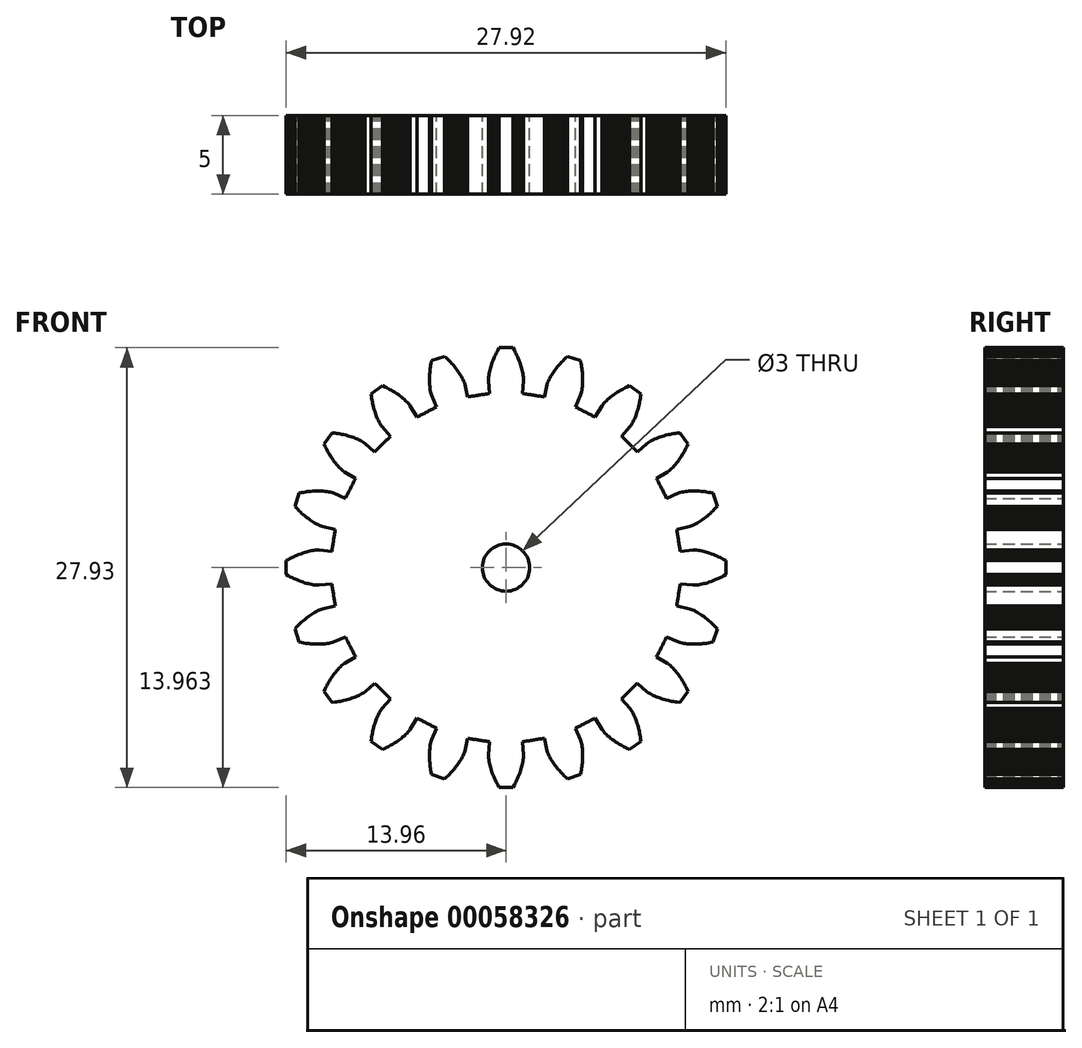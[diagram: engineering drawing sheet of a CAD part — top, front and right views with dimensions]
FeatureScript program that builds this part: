
annotation { "Feature Type Name" : "Feature", "Feature Type Description" : "" }
export const myFeature = defineFeature(function(context is Context, id is Id, definition is map)
    precondition{}
    {
        {
            var Q0;
            Q0=qCreatedBy(makeId("Front.planeOp"),FACE);
            var sketch = newSketch(context, id + "F0", { "sketchPlane" : qUnion([Q0])});
            skLineSegment(sketch, "E0", {"start": v(11.06, 0.88) * mm, "end": v(11.88, 0.8) * mm});
            skLineSegment(sketch, "E1", {"start": v(11.88, 0.8) * mm, "end": v(11.98, 0.8) * mm});
            skLineSegment(sketch, "E2", {"start": v(11.98, 0.8) * mm, "end": v(12.1, 0.8) * mm});
            skLineSegment(sketch, "E3", {"start": v(12.1, 0.8) * mm, "end": v(12.21, 0.82) * mm});
            skLineSegment(sketch, "E4", {"start": v(12.21, 0.82) * mm, "end": v(12.32, 0.84) * mm});
            skLineSegment(sketch, "E5", {"start": v(12.32, 0.84) * mm, "end": v(12.43, 0.86) * mm});
            skLineSegment(sketch, "E6", {"start": v(12.43, 0.86) * mm, "end": v(12.56, 0.9) * mm});
            skLineSegment(sketch, "E7", {"start": v(12.56, 0.9) * mm, "end": v(12.67, 0.92) * mm});
            skLineSegment(sketch, "E8", {"start": v(12.67, 0.92) * mm, "end": v(12.79, 0.95) * mm});
            skLineSegment(sketch, "E9", {"start": v(12.79, 0.95) * mm, "end": v(12.9, 1) * mm});
            skLineSegment(sketch, "E10", {"start": v(12.9, 1) * mm, "end": v(13.03, 1.04) * mm});
            skLineSegment(sketch, "E11", {"start": v(13.03, 1.04) * mm, "end": v(13.17, 1.09) * mm});
            skLineSegment(sketch, "E12", {"start": v(13.17, 1.09) * mm, "end": v(13.3, 1.15) * mm});
            skLineSegment(sketch, "E13", {"start": v(13.3, 1.15) * mm, "end": v(13.4, 1.19) * mm});
            skLineSegment(sketch, "E14", {"start": v(13.4, 1.19) * mm, "end": v(13.5, 1.23) * mm});
            skLineSegment(sketch, "E15", {"start": v(13.5, 1.23) * mm, "end": v(13.6, 1.28) * mm});
            skLineSegment(sketch, "E16", {"start": v(13.6, 1.28) * mm, "end": v(13.7, 1.33) * mm});
            skLineSegment(sketch, "E17", {"start": v(13.7, 1.33) * mm, "end": v(13.81, 1.39) * mm});
            skLineSegment(sketch, "E18", {"start": v(13.81, 1.39) * mm, "end": v(13.96, 1.47) * mm});
            skLineSegment(sketch, "E19", {"start": v(13.96, 1.47) * mm, "end": v(13.96, 2.35) * mm});
            skLineSegment(sketch, "E20", {"start": v(13.96, 2.35) * mm, "end": v(13.81, 2.44) * mm});
            skLineSegment(sketch, "E21", {"start": v(13.81, 2.44) * mm, "end": v(13.7, 2.5) * mm});
            skLineSegment(sketch, "E22", {"start": v(13.7, 2.5) * mm, "end": v(13.6, 2.54) * mm});
            skLineSegment(sketch, "E23", {"start": v(13.6, 2.54) * mm, "end": v(13.5, 2.6) * mm});
            skLineSegment(sketch, "E24", {"start": v(13.5, 2.6) * mm, "end": v(13.4, 2.64) * mm});
            skLineSegment(sketch, "E25", {"start": v(13.4, 2.64) * mm, "end": v(13.3, 2.68) * mm});
            skLineSegment(sketch, "E26", {"start": v(13.3, 2.68) * mm, "end": v(13.17, 2.74) * mm});
            skLineSegment(sketch, "E27", {"start": v(13.17, 2.74) * mm, "end": v(13.03, 2.79) * mm});
            skLineSegment(sketch, "E28", {"start": v(13.03, 2.79) * mm, "end": v(12.9, 2.83) * mm});
            skLineSegment(sketch, "E29", {"start": v(12.9, 2.83) * mm, "end": v(12.79, 2.87) * mm});
            skLineSegment(sketch, "E30", {"start": v(12.79, 2.87) * mm, "end": v(12.67, 2.9) * mm});
            skLineSegment(sketch, "E31", {"start": v(12.67, 2.9) * mm, "end": v(12.56, 2.93) * mm});
            skLineSegment(sketch, "E32", {"start": v(12.56, 2.93) * mm, "end": v(12.43, 2.97) * mm});
            skLineSegment(sketch, "E33", {"start": v(12.43, 2.97) * mm, "end": v(12.32, 2.99) * mm});
            skLineSegment(sketch, "E34", {"start": v(12.32, 2.99) * mm, "end": v(12.21, 3) * mm});
            skLineSegment(sketch, "E35", {"start": v(12.21, 3) * mm, "end": v(12.1, 3.02) * mm});
            skLineSegment(sketch, "E36", {"start": v(12.1, 3.02) * mm, "end": v(11.98, 3.03) * mm});
            skLineSegment(sketch, "E37", {"start": v(11.98, 3.03) * mm, "end": v(11.88, 3.03) * mm});
            skLineSegment(sketch, "E38", {"start": v(11.88, 3.03) * mm, "end": v(11.06, 2.95) * mm});
            skArc(sketch, "E39", {"start": v(11.06, 2.95) * mm, "mid": v(10.95, 3.65) * mm, "end": v(10.84, 4.35) * mm});
            skLineSegment(sketch, "E40", {"start": v(10.84, 4.35) * mm, "end": v(11.64, 4.53) * mm});
            skLineSegment(sketch, "E41", {"start": v(11.64, 4.53) * mm, "end": v(11.74, 4.56) * mm});
            skLineSegment(sketch, "E42", {"start": v(11.74, 4.56) * mm, "end": v(11.85, 4.6) * mm});
            skLineSegment(sketch, "E43", {"start": v(11.85, 4.6) * mm, "end": v(11.95, 4.65) * mm});
            skLineSegment(sketch, "E44", {"start": v(11.95, 4.65) * mm, "end": v(12.05, 4.7) * mm});
            skLineSegment(sketch, "E45", {"start": v(12.05, 4.7) * mm, "end": v(12.15, 4.75) * mm});
            skLineSegment(sketch, "E46", {"start": v(12.15, 4.75) * mm, "end": v(12.27, 4.82) * mm});
            skLineSegment(sketch, "E47", {"start": v(12.27, 4.82) * mm, "end": v(12.36, 4.88) * mm});
            skLineSegment(sketch, "E48", {"start": v(12.36, 4.88) * mm, "end": v(12.46, 4.95) * mm});
            skLineSegment(sketch, "E49", {"start": v(12.46, 4.95) * mm, "end": v(12.56, 5.02) * mm});
            skLineSegment(sketch, "E50", {"start": v(12.56, 5.02) * mm, "end": v(12.67, 5.1) * mm});
            skLineSegment(sketch, "E51", {"start": v(12.67, 5.1) * mm, "end": v(12.78, 5.2) * mm});
            skLineSegment(sketch, "E52", {"start": v(12.78, 5.2) * mm, "end": v(12.9, 5.3) * mm});
            skLineSegment(sketch, "E53", {"start": v(12.9, 5.3) * mm, "end": v(12.97, 5.36) * mm});
            skLineSegment(sketch, "E54", {"start": v(12.97, 5.36) * mm, "end": v(13.05, 5.44) * mm});
            skLineSegment(sketch, "E55", {"start": v(13.05, 5.44) * mm, "end": v(13.13, 5.52) * mm});
            skLineSegment(sketch, "E56", {"start": v(13.13, 5.52) * mm, "end": v(13.22, 5.6) * mm});
            skLineSegment(sketch, "E57", {"start": v(13.22, 5.6) * mm, "end": v(13.3, 5.68) * mm});
            skLineSegment(sketch, "E58", {"start": v(13.3, 5.68) * mm, "end": v(13.42, 5.8) * mm});
            skLineSegment(sketch, "E59", {"start": v(13.42, 5.8) * mm, "end": v(13.14, 6.65) * mm});
            skLineSegment(sketch, "E60", {"start": v(13.14, 6.65) * mm, "end": v(12.98, 6.68) * mm});
            skLineSegment(sketch, "E61", {"start": v(12.98, 6.68) * mm, "end": v(12.86, 6.7) * mm});
            skLineSegment(sketch, "E62", {"start": v(12.86, 6.7) * mm, "end": v(12.74, 6.72) * mm});
            skLineSegment(sketch, "E63", {"start": v(12.74, 6.72) * mm, "end": v(12.63, 6.73) * mm});
            skLineSegment(sketch, "E64", {"start": v(12.63, 6.73) * mm, "end": v(12.52, 6.74) * mm});
            skLineSegment(sketch, "E65", {"start": v(12.52, 6.74) * mm, "end": v(12.42, 6.75) * mm});
            skLineSegment(sketch, "E66", {"start": v(12.42, 6.75) * mm, "end": v(12.27, 6.77) * mm});
            skLineSegment(sketch, "E67", {"start": v(12.27, 6.77) * mm, "end": v(12.12, 6.77) * mm});
            skLineSegment(sketch, "E68", {"start": v(12.12, 6.77) * mm, "end": v(11.99, 6.78) * mm});
            skLineSegment(sketch, "E69", {"start": v(11.99, 6.78) * mm, "end": v(11.86, 6.78) * mm});
            skLineSegment(sketch, "E70", {"start": v(11.86, 6.78) * mm, "end": v(11.74, 6.77) * mm});
            skLineSegment(sketch, "E71", {"start": v(11.74, 6.77) * mm, "end": v(11.63, 6.77) * mm});
            skLineSegment(sketch, "E72", {"start": v(11.63, 6.77) * mm, "end": v(11.5, 6.76) * mm});
            skLineSegment(sketch, "E73", {"start": v(11.5, 6.76) * mm, "end": v(11.38, 6.74) * mm});
            skLineSegment(sketch, "E74", {"start": v(11.38, 6.74) * mm, "end": v(11.28, 6.73) * mm});
            skLineSegment(sketch, "E75", {"start": v(11.28, 6.73) * mm, "end": v(11.17, 6.7) * mm});
            skLineSegment(sketch, "E76", {"start": v(11.17, 6.7) * mm, "end": v(11.05, 6.68) * mm});
            skLineSegment(sketch, "E77", {"start": v(11.05, 6.68) * mm, "end": v(10.96, 6.64) * mm});
            skLineSegment(sketch, "E78", {"start": v(10.96, 6.64) * mm, "end": v(10.2, 6.32) * mm});
            skArc(sketch, "E79", {"start": v(10.2, 6.32) * mm, "mid": v(9.88, 6.95) * mm, "end": v(9.56, 7.58) * mm});
            skLineSegment(sketch, "E80", {"start": v(9.56, 7.58) * mm, "end": v(10.27, 8) * mm});
            skLineSegment(sketch, "E81", {"start": v(10.27, 8) * mm, "end": v(10.35, 8.06) * mm});
            skLineSegment(sketch, "E82", {"start": v(10.35, 8.06) * mm, "end": v(10.44, 8.13) * mm});
            skLineSegment(sketch, "E83", {"start": v(10.44, 8.13) * mm, "end": v(10.52, 8.2) * mm});
            skLineSegment(sketch, "E84", {"start": v(10.52, 8.2) * mm, "end": v(10.6, 8.28) * mm});
            skLineSegment(sketch, "E85", {"start": v(10.6, 8.28) * mm, "end": v(10.68, 8.37) * mm});
            skLineSegment(sketch, "E86", {"start": v(10.68, 8.37) * mm, "end": v(10.77, 8.47) * mm});
            skLineSegment(sketch, "E87", {"start": v(10.77, 8.47) * mm, "end": v(10.84, 8.56) * mm});
            skLineSegment(sketch, "E88", {"start": v(10.84, 8.56) * mm, "end": v(10.9, 8.65) * mm});
            skLineSegment(sketch, "E89", {"start": v(10.9, 8.65) * mm, "end": v(10.98, 8.75) * mm});
            skLineSegment(sketch, "E90", {"start": v(10.98, 8.75) * mm, "end": v(11.06, 8.86) * mm});
            skLineSegment(sketch, "E91", {"start": v(11.06, 8.86) * mm, "end": v(11.14, 8.98) * mm});
            skLineSegment(sketch, "E92", {"start": v(11.14, 8.98) * mm, "end": v(11.22, 9.11) * mm});
            skLineSegment(sketch, "E93", {"start": v(11.22, 9.11) * mm, "end": v(11.27, 9.2) * mm});
            skLineSegment(sketch, "E94", {"start": v(11.27, 9.2) * mm, "end": v(11.32, 9.3) * mm});
            skLineSegment(sketch, "E95", {"start": v(11.32, 9.3) * mm, "end": v(11.38, 9.4) * mm});
            skLineSegment(sketch, "E96", {"start": v(11.38, 9.4) * mm, "end": v(11.43, 9.5) * mm});
            skLineSegment(sketch, "E97", {"start": v(11.43, 9.5) * mm, "end": v(11.48, 9.6) * mm});
            skLineSegment(sketch, "E98", {"start": v(11.48, 9.6) * mm, "end": v(11.56, 9.76) * mm});
            skLineSegment(sketch, "E99", {"start": v(11.56, 9.76) * mm, "end": v(11.04, 10.48) * mm});
            skLineSegment(sketch, "E100", {"start": v(11.04, 10.48) * mm, "end": v(10.87, 10.46) * mm});
            skLineSegment(sketch, "E101", {"start": v(10.87, 10.46) * mm, "end": v(10.75, 10.44) * mm});
            skLineSegment(sketch, "E102", {"start": v(10.75, 10.44) * mm, "end": v(10.64, 10.42) * mm});
            skLineSegment(sketch, "E103", {"start": v(10.64, 10.42) * mm, "end": v(10.52, 10.4) * mm});
            skLineSegment(sketch, "E104", {"start": v(10.52, 10.4) * mm, "end": v(10.42, 10.38) * mm});
            skLineSegment(sketch, "E105", {"start": v(10.42, 10.38) * mm, "end": v(10.31, 10.36) * mm});
            skLineSegment(sketch, "E106", {"start": v(10.31, 10.36) * mm, "end": v(10.17, 10.32) * mm});
            skLineSegment(sketch, "E107", {"start": v(10.17, 10.32) * mm, "end": v(10.03, 10.28) * mm});
            skLineSegment(sketch, "E108", {"start": v(10.03, 10.28) * mm, "end": v(9.9, 10.24) * mm});
            skLineSegment(sketch, "E109", {"start": v(9.9, 10.24) * mm, "end": v(9.78, 10.2) * mm});
            skLineSegment(sketch, "E110", {"start": v(9.78, 10.2) * mm, "end": v(9.67, 10.16) * mm});
            skLineSegment(sketch, "E111", {"start": v(9.67, 10.16) * mm, "end": v(9.56, 10.12) * mm});
            skLineSegment(sketch, "E112", {"start": v(9.56, 10.12) * mm, "end": v(9.44, 10.07) * mm});
            skLineSegment(sketch, "E113", {"start": v(9.44, 10.07) * mm, "end": v(9.33, 10.02) * mm});
            skLineSegment(sketch, "E114", {"start": v(9.33, 10.02) * mm, "end": v(9.24, 9.97) * mm});
            skLineSegment(sketch, "E115", {"start": v(9.24, 9.97) * mm, "end": v(9.14, 9.92) * mm});
            skLineSegment(sketch, "E116", {"start": v(9.14, 9.92) * mm, "end": v(9.04, 9.86) * mm});
            skLineSegment(sketch, "E117", {"start": v(9.04, 9.86) * mm, "end": v(8.96, 9.8) * mm});
            skLineSegment(sketch, "E118", {"start": v(8.96, 9.8) * mm, "end": v(8.34, 9.25) * mm});
            skArc(sketch, "E119", {"start": v(8.34, 9.25) * mm, "mid": v(7.84, 9.75) * mm, "end": v(7.34, 10.25) * mm});
            skLineSegment(sketch, "E120", {"start": v(7.34, 10.25) * mm, "end": v(7.89, 10.87) * mm});
            skLineSegment(sketch, "E121", {"start": v(7.89, 10.87) * mm, "end": v(7.95, 10.95) * mm});
            skLineSegment(sketch, "E122", {"start": v(7.95, 10.95) * mm, "end": v(8, 11.05) * mm});
            skLineSegment(sketch, "E123", {"start": v(8, 11.05) * mm, "end": v(8.06, 11.15) * mm});
            skLineSegment(sketch, "E124", {"start": v(8.06, 11.15) * mm, "end": v(8.1, 11.24) * mm});
            skLineSegment(sketch, "E125", {"start": v(8.1, 11.24) * mm, "end": v(8.16, 11.35) * mm});
            skLineSegment(sketch, "E126", {"start": v(8.16, 11.35) * mm, "end": v(8.21, 11.48) * mm});
            skLineSegment(sketch, "E127", {"start": v(8.21, 11.48) * mm, "end": v(8.25, 11.58) * mm});
            skLineSegment(sketch, "E128", {"start": v(8.25, 11.58) * mm, "end": v(8.3, 11.7) * mm});
            skLineSegment(sketch, "E129", {"start": v(8.3, 11.7) * mm, "end": v(8.33, 11.81) * mm});
            skLineSegment(sketch, "E130", {"start": v(8.33, 11.81) * mm, "end": v(8.37, 11.94) * mm});
            skLineSegment(sketch, "E131", {"start": v(8.37, 11.94) * mm, "end": v(8.4, 12.08) * mm});
            skLineSegment(sketch, "E132", {"start": v(8.4, 12.08) * mm, "end": v(8.44, 12.23) * mm});
            skLineSegment(sketch, "E133", {"start": v(8.44, 12.23) * mm, "end": v(8.47, 12.33) * mm});
            skLineSegment(sketch, "E134", {"start": v(8.47, 12.33) * mm, "end": v(8.49, 12.44) * mm});
            skLineSegment(sketch, "E135", {"start": v(8.49, 12.44) * mm, "end": v(8.5, 12.55) * mm});
            skLineSegment(sketch, "E136", {"start": v(8.5, 12.55) * mm, "end": v(8.53, 12.66) * mm});
            skLineSegment(sketch, "E137", {"start": v(8.53, 12.66) * mm, "end": v(8.54, 12.78) * mm});
            skLineSegment(sketch, "E138", {"start": v(8.54, 12.78) * mm, "end": v(8.56, 12.95) * mm});
            skLineSegment(sketch, "E139", {"start": v(8.56, 12.95) * mm, "end": v(7.85, 13.47) * mm});
            skLineSegment(sketch, "E140", {"start": v(7.85, 13.47) * mm, "end": v(7.7, 13.4) * mm});
            skLineSegment(sketch, "E141", {"start": v(7.7, 13.4) * mm, "end": v(7.59, 13.34) * mm});
            skLineSegment(sketch, "E142", {"start": v(7.59, 13.34) * mm, "end": v(7.49, 13.29) * mm});
            skLineSegment(sketch, "E143", {"start": v(7.49, 13.29) * mm, "end": v(7.39, 13.24) * mm});
            skLineSegment(sketch, "E144", {"start": v(7.39, 13.24) * mm, "end": v(7.3, 13.18) * mm});
            skLineSegment(sketch, "E145", {"start": v(7.3, 13.18) * mm, "end": v(7.2, 13.13) * mm});
            skLineSegment(sketch, "E146", {"start": v(7.2, 13.13) * mm, "end": v(7.07, 13.05) * mm});
            skLineSegment(sketch, "E147", {"start": v(7.07, 13.05) * mm, "end": v(6.95, 12.97) * mm});
            skLineSegment(sketch, "E148", {"start": v(6.95, 12.97) * mm, "end": v(6.84, 12.9) * mm});
            skLineSegment(sketch, "E149", {"start": v(6.84, 12.9) * mm, "end": v(6.74, 12.82) * mm});
            skLineSegment(sketch, "E150", {"start": v(6.74, 12.82) * mm, "end": v(6.64, 12.75) * mm});
            skLineSegment(sketch, "E151", {"start": v(6.64, 12.75) * mm, "end": v(6.56, 12.68) * mm});
            skLineSegment(sketch, "E152", {"start": v(6.56, 12.68) * mm, "end": v(6.46, 12.6) * mm});
            skLineSegment(sketch, "E153", {"start": v(6.46, 12.6) * mm, "end": v(6.37, 12.5) * mm});
            skLineSegment(sketch, "E154", {"start": v(6.37, 12.5) * mm, "end": v(6.3, 12.43) * mm});
            skLineSegment(sketch, "E155", {"start": v(6.3, 12.43) * mm, "end": v(6.22, 12.35) * mm});
            skLineSegment(sketch, "E156", {"start": v(6.22, 12.35) * mm, "end": v(6.14, 12.26) * mm});
            skLineSegment(sketch, "E157", {"start": v(6.14, 12.26) * mm, "end": v(6.08, 12.18) * mm});
            skLineSegment(sketch, "E158", {"start": v(6.08, 12.18) * mm, "end": v(5.66, 11.47) * mm});
            skArc(sketch, "E159", {"start": v(5.66, 11.47) * mm, "mid": v(5.03, 11.8) * mm, "end": v(4.4, 12.11) * mm});
            skLineSegment(sketch, "E160", {"start": v(4.4, 12.11) * mm, "end": v(4.73, 12.87) * mm});
            skLineSegment(sketch, "E161", {"start": v(4.73, 12.87) * mm, "end": v(4.76, 12.97) * mm});
            skLineSegment(sketch, "E162", {"start": v(4.76, 12.97) * mm, "end": v(4.8, 13.08) * mm});
            skLineSegment(sketch, "E163", {"start": v(4.8, 13.08) * mm, "end": v(4.81, 13.19) * mm});
            skLineSegment(sketch, "E164", {"start": v(4.81, 13.19) * mm, "end": v(4.83, 13.3) * mm});
            skLineSegment(sketch, "E165", {"start": v(4.83, 13.3) * mm, "end": v(4.84, 13.41) * mm});
            skLineSegment(sketch, "E166", {"start": v(4.84, 13.41) * mm, "end": v(4.85, 13.55) * mm});
            skLineSegment(sketch, "E167", {"start": v(4.85, 13.55) * mm, "end": v(4.86, 13.66) * mm});
            skLineSegment(sketch, "E168", {"start": v(4.86, 13.66) * mm, "end": v(4.86, 13.78) * mm});
            skLineSegment(sketch, "E169", {"start": v(4.86, 13.78) * mm, "end": v(4.86, 13.9) * mm});
            skLineSegment(sketch, "E170", {"start": v(4.86, 13.9) * mm, "end": v(4.86, 14.04) * mm});
            skLineSegment(sketch, "E171", {"start": v(4.86, 14.04) * mm, "end": v(4.85, 14.18) * mm});
            skLineSegment(sketch, "E172", {"start": v(4.85, 14.18) * mm, "end": v(4.84, 14.33) * mm});
            skLineSegment(sketch, "E173", {"start": v(4.84, 14.33) * mm, "end": v(4.83, 14.44) * mm});
            skLineSegment(sketch, "E174", {"start": v(4.83, 14.44) * mm, "end": v(4.82, 14.54) * mm});
            skLineSegment(sketch, "E175", {"start": v(4.82, 14.54) * mm, "end": v(4.8, 14.66) * mm});
            skLineSegment(sketch, "E176", {"start": v(4.8, 14.66) * mm, "end": v(4.79, 14.77) * mm});
            skLineSegment(sketch, "E177", {"start": v(4.79, 14.77) * mm, "end": v(4.77, 14.89) * mm});
            skLineSegment(sketch, "E178", {"start": v(4.77, 14.89) * mm, "end": v(4.73, 15.06) * mm});
            skLineSegment(sketch, "E179", {"start": v(4.73, 15.06) * mm, "end": v(3.9, 15.33) * mm});
            skLineSegment(sketch, "E180", {"start": v(3.9, 15.33) * mm, "end": v(3.77, 15.21) * mm});
            skLineSegment(sketch, "E181", {"start": v(3.77, 15.21) * mm, "end": v(3.69, 15.13) * mm});
            skLineSegment(sketch, "E182", {"start": v(3.69, 15.13) * mm, "end": v(3.6, 15.05) * mm});
            skLineSegment(sketch, "E183", {"start": v(3.6, 15.05) * mm, "end": v(3.53, 14.96) * mm});
            skLineSegment(sketch, "E184", {"start": v(3.53, 14.96) * mm, "end": v(3.45, 14.88) * mm});
            skLineSegment(sketch, "E185", {"start": v(3.45, 14.88) * mm, "end": v(3.38, 14.8) * mm});
            skLineSegment(sketch, "E186", {"start": v(3.38, 14.8) * mm, "end": v(3.28, 14.7) * mm});
            skLineSegment(sketch, "E187", {"start": v(3.28, 14.7) * mm, "end": v(3.2, 14.58) * mm});
            skLineSegment(sketch, "E188", {"start": v(3.2, 14.58) * mm, "end": v(3.11, 14.47) * mm});
            skLineSegment(sketch, "E189", {"start": v(3.11, 14.47) * mm, "end": v(3.04, 14.37) * mm});
            skLineSegment(sketch, "E190", {"start": v(3.04, 14.37) * mm, "end": v(2.97, 14.27) * mm});
            skLineSegment(sketch, "E191", {"start": v(2.97, 14.27) * mm, "end": v(2.91, 14.18) * mm});
            skLineSegment(sketch, "E192", {"start": v(2.91, 14.18) * mm, "end": v(2.84, 14.06) * mm});
            skLineSegment(sketch, "E193", {"start": v(2.84, 14.06) * mm, "end": v(2.78, 13.96) * mm});
            skLineSegment(sketch, "E194", {"start": v(2.78, 13.96) * mm, "end": v(2.73, 13.86) * mm});
            skLineSegment(sketch, "E195", {"start": v(2.73, 13.86) * mm, "end": v(2.69, 13.76) * mm});
            skLineSegment(sketch, "E196", {"start": v(2.69, 13.76) * mm, "end": v(2.64, 13.65) * mm});
            skLineSegment(sketch, "E197", {"start": v(2.64, 13.65) * mm, "end": v(2.61, 13.56) * mm});
            skLineSegment(sketch, "E198", {"start": v(2.61, 13.56) * mm, "end": v(2.43, 12.76) * mm});
            skArc(sketch, "E199", {"start": v(2.43, 12.76) * mm, "mid": v(1.73, 12.87) * mm, "end": v(1.04, 12.98) * mm});
            skLineSegment(sketch, "E200", {"start": v(1.04, 12.98) * mm, "end": v(1.11, 13.8) * mm});
            skLineSegment(sketch, "E201", {"start": v(1.11, 13.8) * mm, "end": v(1.11, 13.9) * mm});
            skLineSegment(sketch, "E202", {"start": v(1.11, 13.9) * mm, "end": v(1.1, 14.01) * mm});
            skLineSegment(sketch, "E203", {"start": v(1.1, 14.01) * mm, "end": v(1.1, 14.12) * mm});
            skLineSegment(sketch, "E204", {"start": v(1.1, 14.12) * mm, "end": v(1.08, 14.23) * mm});
            skLineSegment(sketch, "E205", {"start": v(1.08, 14.23) * mm, "end": v(1.05, 14.35) * mm});
            skLineSegment(sketch, "E206", {"start": v(1.05, 14.35) * mm, "end": v(1.02, 14.48) * mm});
            skLineSegment(sketch, "E207", {"start": v(1.02, 14.48) * mm, "end": v(1, 14.58) * mm});
            skLineSegment(sketch, "E208", {"start": v(1, 14.58) * mm, "end": v(0.96, 14.7) * mm});
            skLineSegment(sketch, "E209", {"start": v(0.96, 14.7) * mm, "end": v(0.92, 14.82) * mm});
            skLineSegment(sketch, "E210", {"start": v(0.92, 14.82) * mm, "end": v(0.88, 14.95) * mm});
            skLineSegment(sketch, "E211", {"start": v(0.88, 14.95) * mm, "end": v(0.83, 15.08) * mm});
            skLineSegment(sketch, "E212", {"start": v(0.83, 15.08) * mm, "end": v(0.77, 15.22) * mm});
            skLineSegment(sketch, "E213", {"start": v(0.77, 15.22) * mm, "end": v(0.73, 15.32) * mm});
            skLineSegment(sketch, "E214", {"start": v(0.73, 15.32) * mm, "end": v(0.68, 15.42) * mm});
            skLineSegment(sketch, "E215", {"start": v(0.68, 15.42) * mm, "end": v(0.63, 15.52) * mm});
            skLineSegment(sketch, "E216", {"start": v(0.63, 15.52) * mm, "end": v(0.58, 15.62) * mm});
            skLineSegment(sketch, "E217", {"start": v(0.58, 15.62) * mm, "end": v(0.52, 15.73) * mm});
            skLineSegment(sketch, "E218", {"start": v(0.52, 15.73) * mm, "end": v(0.44, 15.88) * mm});
            skLineSegment(sketch, "E219", {"start": v(0.44, 15.88) * mm, "end": v(-0.44, 15.88) * mm});
            skLineSegment(sketch, "E220", {"start": v(-0.44, 15.88) * mm, "end": v(-0.52, 15.73) * mm});
            skLineSegment(sketch, "E221", {"start": v(-0.52, 15.73) * mm, "end": v(-0.58, 15.62) * mm});
            skLineSegment(sketch, "E222", {"start": v(-0.58, 15.62) * mm, "end": v(-0.63, 15.52) * mm});
            skLineSegment(sketch, "E223", {"start": v(-0.63, 15.52) * mm, "end": v(-0.68, 15.42) * mm});
            skLineSegment(sketch, "E224", {"start": v(-0.68, 15.42) * mm, "end": v(-0.73, 15.32) * mm});
            skLineSegment(sketch, "E225", {"start": v(-0.73, 15.32) * mm, "end": v(-0.77, 15.22) * mm});
            skLineSegment(sketch, "E226", {"start": v(-0.77, 15.22) * mm, "end": v(-0.83, 15.08) * mm});
            skLineSegment(sketch, "E227", {"start": v(-0.83, 15.08) * mm, "end": v(-0.88, 14.95) * mm});
            skLineSegment(sketch, "E228", {"start": v(-0.88, 14.95) * mm, "end": v(-0.92, 14.82) * mm});
            skLineSegment(sketch, "E229", {"start": v(-0.92, 14.82) * mm, "end": v(-0.96, 14.7) * mm});
            skLineSegment(sketch, "E230", {"start": v(-0.96, 14.7) * mm, "end": v(-1, 14.58) * mm});
            skLineSegment(sketch, "E231", {"start": v(-1, 14.58) * mm, "end": v(-1.02, 14.48) * mm});
            skLineSegment(sketch, "E232", {"start": v(-1.02, 14.48) * mm, "end": v(-1.05, 14.35) * mm});
            skLineSegment(sketch, "E233", {"start": v(-1.05, 14.35) * mm, "end": v(-1.08, 14.23) * mm});
            skLineSegment(sketch, "E234", {"start": v(-1.08, 14.23) * mm, "end": v(-1.1, 14.12) * mm});
            skLineSegment(sketch, "E235", {"start": v(-1.1, 14.12) * mm, "end": v(-1.1, 14.01) * mm});
            skLineSegment(sketch, "E236", {"start": v(-1.1, 14.01) * mm, "end": v(-1.11, 13.9) * mm});
            skLineSegment(sketch, "E237", {"start": v(-1.11, 13.9) * mm, "end": v(-1.11, 13.8) * mm});
            skLineSegment(sketch, "E238", {"start": v(-1.11, 13.8) * mm, "end": v(-1.04, 12.98) * mm});
            skArc(sketch, "E239", {"start": v(-1.04, 12.98) * mm, "mid": v(-1.73, 12.87) * mm, "end": v(-2.43, 12.76) * mm});
            skLineSegment(sketch, "E240", {"start": v(-2.43, 12.76) * mm, "end": v(-2.61, 13.56) * mm});
            skLineSegment(sketch, "E241", {"start": v(-2.61, 13.56) * mm, "end": v(-2.64, 13.65) * mm});
            skLineSegment(sketch, "E242", {"start": v(-2.64, 13.65) * mm, "end": v(-2.69, 13.76) * mm});
            skLineSegment(sketch, "E243", {"start": v(-2.69, 13.76) * mm, "end": v(-2.73, 13.86) * mm});
            skLineSegment(sketch, "E244", {"start": v(-2.73, 13.86) * mm, "end": v(-2.78, 13.96) * mm});
            skLineSegment(sketch, "E245", {"start": v(-2.78, 13.96) * mm, "end": v(-2.84, 14.06) * mm});
            skLineSegment(sketch, "E246", {"start": v(-2.84, 14.06) * mm, "end": v(-2.91, 14.18) * mm});
            skLineSegment(sketch, "E247", {"start": v(-2.91, 14.18) * mm, "end": v(-2.97, 14.27) * mm});
            skLineSegment(sketch, "E248", {"start": v(-2.97, 14.27) * mm, "end": v(-3.04, 14.37) * mm});
            skLineSegment(sketch, "E249", {"start": v(-3.04, 14.37) * mm, "end": v(-3.11, 14.47) * mm});
            skLineSegment(sketch, "E250", {"start": v(-3.11, 14.47) * mm, "end": v(-3.2, 14.58) * mm});
            skLineSegment(sketch, "E251", {"start": v(-3.2, 14.58) * mm, "end": v(-3.28, 14.7) * mm});
            skLineSegment(sketch, "E252", {"start": v(-3.28, 14.7) * mm, "end": v(-3.38, 14.8) * mm});
            skLineSegment(sketch, "E253", {"start": v(-3.38, 14.8) * mm, "end": v(-3.45, 14.88) * mm});
            skLineSegment(sketch, "E254", {"start": v(-3.45, 14.88) * mm, "end": v(-3.53, 14.96) * mm});
            skLineSegment(sketch, "E255", {"start": v(-3.53, 14.96) * mm, "end": v(-3.6, 15.05) * mm});
            skLineSegment(sketch, "E256", {"start": v(-3.6, 15.05) * mm, "end": v(-3.69, 15.13) * mm});
            skLineSegment(sketch, "E257", {"start": v(-3.69, 15.13) * mm, "end": v(-3.77, 15.21) * mm});
            skLineSegment(sketch, "E258", {"start": v(-3.77, 15.21) * mm, "end": v(-3.9, 15.33) * mm});
            skLineSegment(sketch, "E259", {"start": v(-3.9, 15.33) * mm, "end": v(-4.73, 15.06) * mm});
            skLineSegment(sketch, "E260", {"start": v(-4.73, 15.06) * mm, "end": v(-4.77, 14.89) * mm});
            skLineSegment(sketch, "E261", {"start": v(-4.77, 14.89) * mm, "end": v(-4.79, 14.77) * mm});
            skLineSegment(sketch, "E262", {"start": v(-4.79, 14.77) * mm, "end": v(-4.8, 14.66) * mm});
            skLineSegment(sketch, "E263", {"start": v(-4.8, 14.66) * mm, "end": v(-4.82, 14.54) * mm});
            skLineSegment(sketch, "E264", {"start": v(-4.82, 14.54) * mm, "end": v(-4.83, 14.44) * mm});
            skLineSegment(sketch, "E265", {"start": v(-4.83, 14.44) * mm, "end": v(-4.84, 14.33) * mm});
            skLineSegment(sketch, "E266", {"start": v(-4.84, 14.33) * mm, "end": v(-4.85, 14.18) * mm});
            skLineSegment(sketch, "E267", {"start": v(-4.85, 14.18) * mm, "end": v(-4.86, 14.04) * mm});
            skLineSegment(sketch, "E268", {"start": v(-4.86, 14.04) * mm, "end": v(-4.86, 13.9) * mm});
            skLineSegment(sketch, "E269", {"start": v(-4.86, 13.9) * mm, "end": v(-4.86, 13.78) * mm});
            skLineSegment(sketch, "E270", {"start": v(-4.86, 13.78) * mm, "end": v(-4.86, 13.66) * mm});
            skLineSegment(sketch, "E271", {"start": v(-4.86, 13.66) * mm, "end": v(-4.85, 13.55) * mm});
            skLineSegment(sketch, "E272", {"start": v(-4.85, 13.55) * mm, "end": v(-4.84, 13.41) * mm});
            skLineSegment(sketch, "E273", {"start": v(-4.84, 13.41) * mm, "end": v(-4.83, 13.3) * mm});
            skLineSegment(sketch, "E274", {"start": v(-4.83, 13.3) * mm, "end": v(-4.81, 13.19) * mm});
            skLineSegment(sketch, "E275", {"start": v(-4.81, 13.19) * mm, "end": v(-4.8, 13.08) * mm});
            skLineSegment(sketch, "E276", {"start": v(-4.8, 13.08) * mm, "end": v(-4.76, 12.97) * mm});
            skLineSegment(sketch, "E277", {"start": v(-4.76, 12.97) * mm, "end": v(-4.73, 12.87) * mm});
            skLineSegment(sketch, "E278", {"start": v(-4.73, 12.87) * mm, "end": v(-4.4, 12.11) * mm});
            skArc(sketch, "E279", {"start": v(-4.4, 12.11) * mm, "mid": v(-5.03, 11.8) * mm, "end": v(-5.66, 11.47) * mm});
            skLineSegment(sketch, "E280", {"start": v(-5.66, 11.47) * mm, "end": v(-6.08, 12.18) * mm});
            skLineSegment(sketch, "E281", {"start": v(-6.08, 12.18) * mm, "end": v(-6.14, 12.26) * mm});
            skLineSegment(sketch, "E282", {"start": v(-6.14, 12.26) * mm, "end": v(-6.22, 12.35) * mm});
            skLineSegment(sketch, "E283", {"start": v(-6.22, 12.35) * mm, "end": v(-6.3, 12.43) * mm});
            skLineSegment(sketch, "E284", {"start": v(-6.3, 12.43) * mm, "end": v(-6.37, 12.5) * mm});
            skLineSegment(sketch, "E285", {"start": v(-6.37, 12.5) * mm, "end": v(-6.46, 12.6) * mm});
            skLineSegment(sketch, "E286", {"start": v(-6.46, 12.6) * mm, "end": v(-6.56, 12.68) * mm});
            skLineSegment(sketch, "E287", {"start": v(-6.56, 12.68) * mm, "end": v(-6.64, 12.75) * mm});
            skLineSegment(sketch, "E288", {"start": v(-6.64, 12.75) * mm, "end": v(-6.74, 12.82) * mm});
            skLineSegment(sketch, "E289", {"start": v(-6.74, 12.82) * mm, "end": v(-6.84, 12.9) * mm});
            skLineSegment(sketch, "E290", {"start": v(-6.84, 12.9) * mm, "end": v(-6.95, 12.97) * mm});
            skLineSegment(sketch, "E291", {"start": v(-6.95, 12.97) * mm, "end": v(-7.07, 13.05) * mm});
            skLineSegment(sketch, "E292", {"start": v(-7.07, 13.05) * mm, "end": v(-7.2, 13.13) * mm});
            skLineSegment(sketch, "E293", {"start": v(-7.2, 13.13) * mm, "end": v(-7.3, 13.18) * mm});
            skLineSegment(sketch, "E294", {"start": v(-7.3, 13.18) * mm, "end": v(-7.39, 13.24) * mm});
            skLineSegment(sketch, "E295", {"start": v(-7.39, 13.24) * mm, "end": v(-7.49, 13.29) * mm});
            skLineSegment(sketch, "E296", {"start": v(-7.49, 13.29) * mm, "end": v(-7.59, 13.34) * mm});
            skLineSegment(sketch, "E297", {"start": v(-7.59, 13.34) * mm, "end": v(-7.7, 13.4) * mm});
            skLineSegment(sketch, "E298", {"start": v(-7.7, 13.4) * mm, "end": v(-7.85, 13.47) * mm});
            skLineSegment(sketch, "E299", {"start": v(-7.85, 13.47) * mm, "end": v(-8.56, 12.95) * mm});
            skLineSegment(sketch, "E300", {"start": v(-8.56, 12.95) * mm, "end": v(-8.54, 12.78) * mm});
            skLineSegment(sketch, "E301", {"start": v(-8.54, 12.78) * mm, "end": v(-8.53, 12.66) * mm});
            skLineSegment(sketch, "E302", {"start": v(-8.53, 12.66) * mm, "end": v(-8.5, 12.55) * mm});
            skLineSegment(sketch, "E303", {"start": v(-8.5, 12.55) * mm, "end": v(-8.49, 12.44) * mm});
            skLineSegment(sketch, "E304", {"start": v(-8.49, 12.44) * mm, "end": v(-8.47, 12.33) * mm});
            skLineSegment(sketch, "E305", {"start": v(-8.47, 12.33) * mm, "end": v(-8.44, 12.23) * mm});
            skLineSegment(sketch, "E306", {"start": v(-8.44, 12.23) * mm, "end": v(-8.4, 12.08) * mm});
            skLineSegment(sketch, "E307", {"start": v(-8.4, 12.08) * mm, "end": v(-8.37, 11.94) * mm});
            skLineSegment(sketch, "E308", {"start": v(-8.37, 11.94) * mm, "end": v(-8.33, 11.81) * mm});
            skLineSegment(sketch, "E309", {"start": v(-8.33, 11.81) * mm, "end": v(-8.3, 11.7) * mm});
            skLineSegment(sketch, "E310", {"start": v(-8.3, 11.7) * mm, "end": v(-8.25, 11.58) * mm});
            skLineSegment(sketch, "E311", {"start": v(-8.25, 11.58) * mm, "end": v(-8.21, 11.48) * mm});
            skLineSegment(sketch, "E312", {"start": v(-8.21, 11.48) * mm, "end": v(-8.16, 11.35) * mm});
            skLineSegment(sketch, "E313", {"start": v(-8.16, 11.35) * mm, "end": v(-8.1, 11.24) * mm});
            skLineSegment(sketch, "E314", {"start": v(-8.1, 11.24) * mm, "end": v(-8.06, 11.15) * mm});
            skLineSegment(sketch, "E315", {"start": v(-8.06, 11.15) * mm, "end": v(-8, 11.05) * mm});
            skLineSegment(sketch, "E316", {"start": v(-8, 11.05) * mm, "end": v(-7.95, 10.95) * mm});
            skLineSegment(sketch, "E317", {"start": v(-7.95, 10.95) * mm, "end": v(-7.89, 10.87) * mm});
            skLineSegment(sketch, "E318", {"start": v(-7.89, 10.87) * mm, "end": v(-7.34, 10.25) * mm});
            skArc(sketch, "E319", {"start": v(-7.34, 10.25) * mm, "mid": v(-7.84, 9.75) * mm, "end": v(-8.34, 9.25) * mm});
            skLineSegment(sketch, "E320", {"start": v(-8.34, 9.25) * mm, "end": v(-8.96, 9.8) * mm});
            skLineSegment(sketch, "E321", {"start": v(-8.96, 9.8) * mm, "end": v(-9.04, 9.86) * mm});
            skLineSegment(sketch, "E322", {"start": v(-9.04, 9.86) * mm, "end": v(-9.14, 9.92) * mm});
            skLineSegment(sketch, "E323", {"start": v(-9.14, 9.92) * mm, "end": v(-9.24, 9.97) * mm});
            skLineSegment(sketch, "E324", {"start": v(-9.24, 9.97) * mm, "end": v(-9.33, 10.02) * mm});
            skLineSegment(sketch, "E325", {"start": v(-9.33, 10.02) * mm, "end": v(-9.44, 10.07) * mm});
            skLineSegment(sketch, "E326", {"start": v(-9.44, 10.07) * mm, "end": v(-9.56, 10.12) * mm});
            skLineSegment(sketch, "E327", {"start": v(-9.56, 10.12) * mm, "end": v(-9.67, 10.16) * mm});
            skLineSegment(sketch, "E328", {"start": v(-9.67, 10.16) * mm, "end": v(-9.78, 10.2) * mm});
            skLineSegment(sketch, "E329", {"start": v(-9.78, 10.2) * mm, "end": v(-9.9, 10.24) * mm});
            skLineSegment(sketch, "E330", {"start": v(-9.9, 10.24) * mm, "end": v(-10.03, 10.28) * mm});
            skLineSegment(sketch, "E331", {"start": v(-10.03, 10.28) * mm, "end": v(-10.17, 10.32) * mm});
            skLineSegment(sketch, "E332", {"start": v(-10.17, 10.32) * mm, "end": v(-10.31, 10.36) * mm});
            skLineSegment(sketch, "E333", {"start": v(-10.31, 10.36) * mm, "end": v(-10.42, 10.38) * mm});
            skLineSegment(sketch, "E334", {"start": v(-10.42, 10.38) * mm, "end": v(-10.52, 10.4) * mm});
            skLineSegment(sketch, "E335", {"start": v(-10.52, 10.4) * mm, "end": v(-10.64, 10.42) * mm});
            skLineSegment(sketch, "E336", {"start": v(-10.64, 10.42) * mm, "end": v(-10.75, 10.44) * mm});
            skLineSegment(sketch, "E337", {"start": v(-10.75, 10.44) * mm, "end": v(-10.87, 10.46) * mm});
            skLineSegment(sketch, "E338", {"start": v(-10.87, 10.46) * mm, "end": v(-11.04, 10.48) * mm});
            skLineSegment(sketch, "E339", {"start": v(-11.04, 10.48) * mm, "end": v(-11.56, 9.76) * mm});
            skLineSegment(sketch, "E340", {"start": v(-11.56, 9.76) * mm, "end": v(-11.48, 9.6) * mm});
            skLineSegment(sketch, "E341", {"start": v(-11.48, 9.6) * mm, "end": v(-11.43, 9.5) * mm});
            skLineSegment(sketch, "E342", {"start": v(-11.43, 9.5) * mm, "end": v(-11.38, 9.4) * mm});
            skLineSegment(sketch, "E343", {"start": v(-11.38, 9.4) * mm, "end": v(-11.32, 9.3) * mm});
            skLineSegment(sketch, "E344", {"start": v(-11.32, 9.3) * mm, "end": v(-11.27, 9.2) * mm});
            skLineSegment(sketch, "E345", {"start": v(-11.27, 9.2) * mm, "end": v(-11.22, 9.11) * mm});
            skLineSegment(sketch, "E346", {"start": v(-11.22, 9.11) * mm, "end": v(-11.14, 8.98) * mm});
            skLineSegment(sketch, "E347", {"start": v(-11.14, 8.98) * mm, "end": v(-11.06, 8.86) * mm});
            skLineSegment(sketch, "E348", {"start": v(-11.06, 8.86) * mm, "end": v(-10.98, 8.75) * mm});
            skLineSegment(sketch, "E349", {"start": v(-10.98, 8.75) * mm, "end": v(-10.9, 8.65) * mm});
            skLineSegment(sketch, "E350", {"start": v(-10.9, 8.65) * mm, "end": v(-10.84, 8.56) * mm});
            skLineSegment(sketch, "E351", {"start": v(-10.84, 8.56) * mm, "end": v(-10.77, 8.47) * mm});
            skLineSegment(sketch, "E352", {"start": v(-10.77, 8.47) * mm, "end": v(-10.68, 8.37) * mm});
            skLineSegment(sketch, "E353", {"start": v(-10.68, 8.37) * mm, "end": v(-10.6, 8.28) * mm});
            skLineSegment(sketch, "E354", {"start": v(-10.6, 8.28) * mm, "end": v(-10.52, 8.2) * mm});
            skLineSegment(sketch, "E355", {"start": v(-10.52, 8.2) * mm, "end": v(-10.44, 8.13) * mm});
            skLineSegment(sketch, "E356", {"start": v(-10.44, 8.13) * mm, "end": v(-10.35, 8.06) * mm});
            skLineSegment(sketch, "E357", {"start": v(-10.35, 8.06) * mm, "end": v(-10.27, 8) * mm});
            skLineSegment(sketch, "E358", {"start": v(-10.27, 8) * mm, "end": v(-9.56, 7.58) * mm});
            skArc(sketch, "E359", {"start": v(-9.56, 7.58) * mm, "mid": v(-9.88, 6.95) * mm, "end": v(-10.2, 6.32) * mm});
            skLineSegment(sketch, "E360", {"start": v(-10.2, 6.32) * mm, "end": v(-10.96, 6.64) * mm});
            skLineSegment(sketch, "E361", {"start": v(-10.96, 6.64) * mm, "end": v(-11.05, 6.68) * mm});
            skLineSegment(sketch, "E362", {"start": v(-11.05, 6.68) * mm, "end": v(-11.17, 6.7) * mm});
            skLineSegment(sketch, "E363", {"start": v(-11.17, 6.7) * mm, "end": v(-11.28, 6.73) * mm});
            skLineSegment(sketch, "E364", {"start": v(-11.28, 6.73) * mm, "end": v(-11.38, 6.74) * mm});
            skLineSegment(sketch, "E365", {"start": v(-11.38, 6.74) * mm, "end": v(-11.5, 6.76) * mm});
            skLineSegment(sketch, "E366", {"start": v(-11.5, 6.76) * mm, "end": v(-11.63, 6.77) * mm});
            skLineSegment(sketch, "E367", {"start": v(-11.63, 6.77) * mm, "end": v(-11.74, 6.77) * mm});
            skLineSegment(sketch, "E368", {"start": v(-11.74, 6.77) * mm, "end": v(-11.86, 6.78) * mm});
            skLineSegment(sketch, "E369", {"start": v(-11.86, 6.78) * mm, "end": v(-11.99, 6.78) * mm});
            skLineSegment(sketch, "E370", {"start": v(-11.99, 6.78) * mm, "end": v(-12.12, 6.77) * mm});
            skLineSegment(sketch, "E371", {"start": v(-12.12, 6.77) * mm, "end": v(-12.27, 6.77) * mm});
            skLineSegment(sketch, "E372", {"start": v(-12.27, 6.77) * mm, "end": v(-12.42, 6.75) * mm});
            skLineSegment(sketch, "E373", {"start": v(-12.42, 6.75) * mm, "end": v(-12.52, 6.74) * mm});
            skLineSegment(sketch, "E374", {"start": v(-12.52, 6.74) * mm, "end": v(-12.63, 6.73) * mm});
            skLineSegment(sketch, "E375", {"start": v(-12.63, 6.73) * mm, "end": v(-12.74, 6.72) * mm});
            skLineSegment(sketch, "E376", {"start": v(-12.74, 6.72) * mm, "end": v(-12.86, 6.7) * mm});
            skLineSegment(sketch, "E377", {"start": v(-12.86, 6.7) * mm, "end": v(-12.98, 6.68) * mm});
            skLineSegment(sketch, "E378", {"start": v(-12.98, 6.68) * mm, "end": v(-13.14, 6.65) * mm});
            skLineSegment(sketch, "E379", {"start": v(-13.14, 6.65) * mm, "end": v(-13.42, 5.8) * mm});
            skLineSegment(sketch, "E380", {"start": v(-13.42, 5.8) * mm, "end": v(-13.3, 5.68) * mm});
            skLineSegment(sketch, "E381", {"start": v(-13.3, 5.68) * mm, "end": v(-13.22, 5.6) * mm});
            skLineSegment(sketch, "E382", {"start": v(-13.22, 5.6) * mm, "end": v(-13.13, 5.52) * mm});
            skLineSegment(sketch, "E383", {"start": v(-13.13, 5.52) * mm, "end": v(-13.05, 5.44) * mm});
            skLineSegment(sketch, "E384", {"start": v(-13.05, 5.44) * mm, "end": v(-12.97, 5.36) * mm});
            skLineSegment(sketch, "E385", {"start": v(-12.97, 5.36) * mm, "end": v(-12.9, 5.3) * mm});
            skLineSegment(sketch, "E386", {"start": v(-12.9, 5.3) * mm, "end": v(-12.78, 5.2) * mm});
            skLineSegment(sketch, "E387", {"start": v(-12.78, 5.2) * mm, "end": v(-12.67, 5.1) * mm});
            skLineSegment(sketch, "E388", {"start": v(-12.67, 5.1) * mm, "end": v(-12.56, 5.02) * mm});
            skLineSegment(sketch, "E389", {"start": v(-12.56, 5.02) * mm, "end": v(-12.46, 4.95) * mm});
            skLineSegment(sketch, "E390", {"start": v(-12.46, 4.95) * mm, "end": v(-12.36, 4.88) * mm});
            skLineSegment(sketch, "E391", {"start": v(-12.36, 4.88) * mm, "end": v(-12.27, 4.82) * mm});
            skLineSegment(sketch, "E392", {"start": v(-12.27, 4.82) * mm, "end": v(-12.15, 4.75) * mm});
            skLineSegment(sketch, "E393", {"start": v(-12.15, 4.75) * mm, "end": v(-12.05, 4.7) * mm});
            skLineSegment(sketch, "E394", {"start": v(-12.05, 4.7) * mm, "end": v(-11.95, 4.65) * mm});
            skLineSegment(sketch, "E395", {"start": v(-11.95, 4.65) * mm, "end": v(-11.85, 4.6) * mm});
            skLineSegment(sketch, "E396", {"start": v(-11.85, 4.6) * mm, "end": v(-11.74, 4.56) * mm});
            skLineSegment(sketch, "E397", {"start": v(-11.74, 4.56) * mm, "end": v(-11.64, 4.53) * mm});
            skLineSegment(sketch, "E398", {"start": v(-11.64, 4.53) * mm, "end": v(-10.84, 4.35) * mm});
            skArc(sketch, "E399", {"start": v(-10.84, 4.35) * mm, "mid": v(-10.95, 3.65) * mm, "end": v(-11.06, 2.95) * mm});
            skLineSegment(sketch, "E400", {"start": v(-11.06, 2.95) * mm, "end": v(-11.88, 3.03) * mm});
            skLineSegment(sketch, "E401", {"start": v(-11.88, 3.03) * mm, "end": v(-11.98, 3.03) * mm});
            skLineSegment(sketch, "E402", {"start": v(-11.98, 3.03) * mm, "end": v(-12.1, 3.02) * mm});
            skLineSegment(sketch, "E403", {"start": v(-12.1, 3.02) * mm, "end": v(-12.21, 3) * mm});
            skLineSegment(sketch, "E404", {"start": v(-12.21, 3) * mm, "end": v(-12.32, 2.99) * mm});
            skLineSegment(sketch, "E405", {"start": v(-12.32, 2.99) * mm, "end": v(-12.43, 2.97) * mm});
            skLineSegment(sketch, "E406", {"start": v(-12.43, 2.97) * mm, "end": v(-12.56, 2.93) * mm});
            skLineSegment(sketch, "E407", {"start": v(-12.56, 2.93) * mm, "end": v(-12.67, 2.9) * mm});
            skLineSegment(sketch, "E408", {"start": v(-12.67, 2.9) * mm, "end": v(-12.79, 2.87) * mm});
            skLineSegment(sketch, "E409", {"start": v(-12.79, 2.87) * mm, "end": v(-12.9, 2.83) * mm});
            skLineSegment(sketch, "E410", {"start": v(-12.9, 2.83) * mm, "end": v(-13.03, 2.79) * mm});
            skLineSegment(sketch, "E411", {"start": v(-13.03, 2.79) * mm, "end": v(-13.17, 2.74) * mm});
            skLineSegment(sketch, "E412", {"start": v(-13.17, 2.74) * mm, "end": v(-13.3, 2.68) * mm});
            skLineSegment(sketch, "E413", {"start": v(-13.3, 2.68) * mm, "end": v(-13.4, 2.64) * mm});
            skLineSegment(sketch, "E414", {"start": v(-13.4, 2.64) * mm, "end": v(-13.5, 2.6) * mm});
            skLineSegment(sketch, "E415", {"start": v(-13.5, 2.6) * mm, "end": v(-13.6, 2.54) * mm});
            skLineSegment(sketch, "E416", {"start": v(-13.6, 2.54) * mm, "end": v(-13.7, 2.5) * mm});
            skLineSegment(sketch, "E417", {"start": v(-13.7, 2.5) * mm, "end": v(-13.81, 2.44) * mm});
            skLineSegment(sketch, "E418", {"start": v(-13.81, 2.44) * mm, "end": v(-13.96, 2.35) * mm});
            skLineSegment(sketch, "E419", {"start": v(-13.96, 2.35) * mm, "end": v(-13.96, 1.47) * mm});
            skLineSegment(sketch, "E420", {"start": v(-13.96, 1.47) * mm, "end": v(-13.81, 1.39) * mm});
            skLineSegment(sketch, "E421", {"start": v(-13.81, 1.39) * mm, "end": v(-13.7, 1.33) * mm});
            skLineSegment(sketch, "E422", {"start": v(-13.7, 1.33) * mm, "end": v(-13.6, 1.28) * mm});
            skLineSegment(sketch, "E423", {"start": v(-13.6, 1.28) * mm, "end": v(-13.5, 1.23) * mm});
            skLineSegment(sketch, "E424", {"start": v(-13.5, 1.23) * mm, "end": v(-13.4, 1.19) * mm});
            skLineSegment(sketch, "E425", {"start": v(-13.4, 1.19) * mm, "end": v(-13.3, 1.15) * mm});
            skLineSegment(sketch, "E426", {"start": v(-13.3, 1.15) * mm, "end": v(-13.17, 1.09) * mm});
            skLineSegment(sketch, "E427", {"start": v(-13.17, 1.09) * mm, "end": v(-13.03, 1.04) * mm});
            skLineSegment(sketch, "E428", {"start": v(-13.03, 1.04) * mm, "end": v(-12.9, 1) * mm});
            skLineSegment(sketch, "E429", {"start": v(-12.9, 1) * mm, "end": v(-12.79, 0.95) * mm});
            skLineSegment(sketch, "E430", {"start": v(-12.79, 0.95) * mm, "end": v(-12.67, 0.92) * mm});
            skLineSegment(sketch, "E431", {"start": v(-12.67, 0.92) * mm, "end": v(-12.56, 0.9) * mm});
            skLineSegment(sketch, "E432", {"start": v(-12.56, 0.9) * mm, "end": v(-12.43, 0.86) * mm});
            skLineSegment(sketch, "E433", {"start": v(-12.43, 0.86) * mm, "end": v(-12.32, 0.84) * mm});
            skLineSegment(sketch, "E434", {"start": v(-12.32, 0.84) * mm, "end": v(-12.21, 0.82) * mm});
            skLineSegment(sketch, "E435", {"start": v(-12.21, 0.82) * mm, "end": v(-12.1, 0.8) * mm});
            skLineSegment(sketch, "E436", {"start": v(-12.1, 0.8) * mm, "end": v(-11.98, 0.8) * mm});
            skLineSegment(sketch, "E437", {"start": v(-11.98, 0.8) * mm, "end": v(-11.88, 0.8) * mm});
            skLineSegment(sketch, "E438", {"start": v(-11.88, 0.8) * mm, "end": v(-11.06, 0.88) * mm});
            skArc(sketch, "E439", {"start": v(-11.06, 0.88) * mm, "mid": v(-10.95, 0.18) * mm, "end": v(-10.84, -0.52) * mm});
            skLineSegment(sketch, "E440", {"start": v(-10.84, -0.52) * mm, "end": v(-11.64, -0.7) * mm});
            skLineSegment(sketch, "E441", {"start": v(-11.64, -0.7) * mm, "end": v(-11.74, -0.73) * mm});
            skLineSegment(sketch, "E442", {"start": v(-11.74, -0.73) * mm, "end": v(-11.85, -0.77) * mm});
            skLineSegment(sketch, "E443", {"start": v(-11.85, -0.77) * mm, "end": v(-11.95, -0.82) * mm});
            skLineSegment(sketch, "E444", {"start": v(-11.95, -0.82) * mm, "end": v(-12.05, -0.87) * mm});
            skLineSegment(sketch, "E445", {"start": v(-12.05, -0.87) * mm, "end": v(-12.15, -0.93) * mm});
            skLineSegment(sketch, "E446", {"start": v(-12.15, -0.93) * mm, "end": v(-12.27, -1) * mm});
            skLineSegment(sketch, "E447", {"start": v(-12.27, -1) * mm, "end": v(-12.36, -1.06) * mm});
            skLineSegment(sketch, "E448", {"start": v(-12.36, -1.06) * mm, "end": v(-12.46, -1.13) * mm});
            skLineSegment(sketch, "E449", {"start": v(-12.46, -1.13) * mm, "end": v(-12.56, -1.2) * mm});
            skLineSegment(sketch, "E450", {"start": v(-12.56, -1.2) * mm, "end": v(-12.67, -1.28) * mm});
            skLineSegment(sketch, "E451", {"start": v(-12.67, -1.28) * mm, "end": v(-12.78, -1.37) * mm});
            skLineSegment(sketch, "E452", {"start": v(-12.78, -1.37) * mm, "end": v(-12.9, -1.47) * mm});
            skLineSegment(sketch, "E453", {"start": v(-12.9, -1.47) * mm, "end": v(-12.97, -1.54) * mm});
            skLineSegment(sketch, "E454", {"start": v(-12.97, -1.54) * mm, "end": v(-13.05, -1.61) * mm});
            skLineSegment(sketch, "E455", {"start": v(-13.05, -1.61) * mm, "end": v(-13.13, -1.7) * mm});
            skLineSegment(sketch, "E456", {"start": v(-13.13, -1.7) * mm, "end": v(-13.22, -1.77) * mm});
            skLineSegment(sketch, "E457", {"start": v(-13.22, -1.77) * mm, "end": v(-13.3, -1.86) * mm});
            skLineSegment(sketch, "E458", {"start": v(-13.3, -1.86) * mm, "end": v(-13.42, -1.98) * mm});
            skLineSegment(sketch, "E459", {"start": v(-13.42, -1.98) * mm, "end": v(-13.14, -2.82) * mm});
            skLineSegment(sketch, "E460", {"start": v(-13.14, -2.82) * mm, "end": v(-12.98, -2.85) * mm});
            skLineSegment(sketch, "E461", {"start": v(-12.98, -2.85) * mm, "end": v(-12.86, -2.87) * mm});
            skLineSegment(sketch, "E462", {"start": v(-12.86, -2.87) * mm, "end": v(-12.74, -2.9) * mm});
            skLineSegment(sketch, "E463", {"start": v(-12.74, -2.9) * mm, "end": v(-12.63, -2.9) * mm});
            skLineSegment(sketch, "E464", {"start": v(-12.63, -2.9) * mm, "end": v(-12.52, -2.92) * mm});
            skLineSegment(sketch, "E465", {"start": v(-12.52, -2.92) * mm, "end": v(-12.42, -2.93) * mm});
            skLineSegment(sketch, "E466", {"start": v(-12.42, -2.93) * mm, "end": v(-12.27, -2.94) * mm});
            skLineSegment(sketch, "E467", {"start": v(-12.27, -2.94) * mm, "end": v(-12.12, -2.95) * mm});
            skLineSegment(sketch, "E468", {"start": v(-12.12, -2.95) * mm, "end": v(-11.99, -2.95) * mm});
            skLineSegment(sketch, "E469", {"start": v(-11.99, -2.95) * mm, "end": v(-11.86, -2.95) * mm});
            skLineSegment(sketch, "E470", {"start": v(-11.86, -2.95) * mm, "end": v(-11.74, -2.95) * mm});
            skLineSegment(sketch, "E471", {"start": v(-11.74, -2.95) * mm, "end": v(-11.63, -2.94) * mm});
            skLineSegment(sketch, "E472", {"start": v(-11.63, -2.94) * mm, "end": v(-11.5, -2.93) * mm});
            skLineSegment(sketch, "E473", {"start": v(-11.5, -2.93) * mm, "end": v(-11.38, -2.92) * mm});
            skLineSegment(sketch, "E474", {"start": v(-11.38, -2.92) * mm, "end": v(-11.28, -2.9) * mm});
            skLineSegment(sketch, "E475", {"start": v(-11.28, -2.9) * mm, "end": v(-11.17, -2.88) * mm});
            skLineSegment(sketch, "E476", {"start": v(-11.17, -2.88) * mm, "end": v(-11.05, -2.85) * mm});
            skLineSegment(sketch, "E477", {"start": v(-11.05, -2.85) * mm, "end": v(-10.96, -2.82) * mm});
            skLineSegment(sketch, "E478", {"start": v(-10.96, -2.82) * mm, "end": v(-10.2, -2.5) * mm});
            skArc(sketch, "E479", {"start": v(-10.2, -2.5) * mm, "mid": v(-9.88, -3.12) * mm, "end": v(-9.56, -3.75) * mm});
            skLineSegment(sketch, "E480", {"start": v(-9.56, -3.75) * mm, "end": v(-10.27, -4.17) * mm});
            skLineSegment(sketch, "E481", {"start": v(-10.27, -4.17) * mm, "end": v(-10.35, -4.23) * mm});
            skLineSegment(sketch, "E482", {"start": v(-10.35, -4.23) * mm, "end": v(-10.44, -4.3) * mm});
            skLineSegment(sketch, "E483", {"start": v(-10.44, -4.3) * mm, "end": v(-10.52, -4.38) * mm});
            skLineSegment(sketch, "E484", {"start": v(-10.52, -4.38) * mm, "end": v(-10.6, -4.46) * mm});
            skLineSegment(sketch, "E485", {"start": v(-10.6, -4.46) * mm, "end": v(-10.68, -4.54) * mm});
            skLineSegment(sketch, "E486", {"start": v(-10.68, -4.54) * mm, "end": v(-10.77, -4.65) * mm});
            skLineSegment(sketch, "E487", {"start": v(-10.77, -4.65) * mm, "end": v(-10.84, -4.73) * mm});
            skLineSegment(sketch, "E488", {"start": v(-10.84, -4.73) * mm, "end": v(-10.9, -4.83) * mm});
            skLineSegment(sketch, "E489", {"start": v(-10.9, -4.83) * mm, "end": v(-10.98, -4.93) * mm});
            skLineSegment(sketch, "E490", {"start": v(-10.98, -4.93) * mm, "end": v(-11.06, -5.04) * mm});
            skLineSegment(sketch, "E491", {"start": v(-11.06, -5.04) * mm, "end": v(-11.14, -5.16) * mm});
            skLineSegment(sketch, "E492", {"start": v(-11.14, -5.16) * mm, "end": v(-11.22, -5.29) * mm});
            skLineSegment(sketch, "E493", {"start": v(-11.22, -5.29) * mm, "end": v(-11.27, -5.38) * mm});
            skLineSegment(sketch, "E494", {"start": v(-11.27, -5.38) * mm, "end": v(-11.32, -5.47) * mm});
            skLineSegment(sketch, "E495", {"start": v(-11.32, -5.47) * mm, "end": v(-11.38, -5.57) * mm});
            skLineSegment(sketch, "E496", {"start": v(-11.38, -5.57) * mm, "end": v(-11.43, -5.68) * mm});
            skLineSegment(sketch, "E497", {"start": v(-11.43, -5.68) * mm, "end": v(-11.48, -5.78) * mm});
            skLineSegment(sketch, "E498", {"start": v(-11.48, -5.78) * mm, "end": v(-11.56, -5.94) * mm});
            skLineSegment(sketch, "E499", {"start": v(-11.56, -5.94) * mm, "end": v(-11.04, -6.65) * mm});
            skLineSegment(sketch, "E500", {"start": v(-11.04, -6.65) * mm, "end": v(-10.87, -6.63) * mm});
            skLineSegment(sketch, "E501", {"start": v(-10.87, -6.63) * mm, "end": v(-10.75, -6.61) * mm});
            skLineSegment(sketch, "E502", {"start": v(-10.75, -6.61) * mm, "end": v(-10.64, -6.6) * mm});
            skLineSegment(sketch, "E503", {"start": v(-10.64, -6.6) * mm, "end": v(-10.52, -6.57) * mm});
            skLineSegment(sketch, "E504", {"start": v(-10.52, -6.57) * mm, "end": v(-10.42, -6.55) * mm});
            skLineSegment(sketch, "E505", {"start": v(-10.42, -6.55) * mm, "end": v(-10.31, -6.53) * mm});
            skLineSegment(sketch, "E506", {"start": v(-10.31, -6.53) * mm, "end": v(-10.17, -6.5) * mm});
            skLineSegment(sketch, "E507", {"start": v(-10.17, -6.5) * mm, "end": v(-10.03, -6.46) * mm});
            skLineSegment(sketch, "E508", {"start": v(-10.03, -6.46) * mm, "end": v(-9.9, -6.42) * mm});
            skLineSegment(sketch, "E509", {"start": v(-9.9, -6.42) * mm, "end": v(-9.78, -6.38) * mm});
            skLineSegment(sketch, "E510", {"start": v(-9.78, -6.38) * mm, "end": v(-9.67, -6.34) * mm});
            skLineSegment(sketch, "E511", {"start": v(-9.67, -6.34) * mm, "end": v(-9.56, -6.3) * mm});
            skLineSegment(sketch, "E512", {"start": v(-9.56, -6.3) * mm, "end": v(-9.44, -6.25) * mm});
            skLineSegment(sketch, "E513", {"start": v(-9.44, -6.25) * mm, "end": v(-9.33, -6.2) * mm});
            skLineSegment(sketch, "E514", {"start": v(-9.33, -6.2) * mm, "end": v(-9.24, -6.15) * mm});
            skLineSegment(sketch, "E515", {"start": v(-9.24, -6.15) * mm, "end": v(-9.14, -6.1) * mm});
            skLineSegment(sketch, "E516", {"start": v(-9.14, -6.1) * mm, "end": v(-9.04, -6.03) * mm});
            skLineSegment(sketch, "E517", {"start": v(-9.04, -6.03) * mm, "end": v(-8.96, -5.97) * mm});
            skLineSegment(sketch, "E518", {"start": v(-8.96, -5.97) * mm, "end": v(-8.34, -5.43) * mm});
            skArc(sketch, "E519", {"start": v(-8.34, -5.43) * mm, "mid": v(-7.84, -5.93) * mm, "end": v(-7.34, -6.43) * mm});
            skLineSegment(sketch, "E520", {"start": v(-7.34, -6.43) * mm, "end": v(-7.89, -7.05) * mm});
            skLineSegment(sketch, "E521", {"start": v(-7.89, -7.05) * mm, "end": v(-7.95, -7.13) * mm});
            skLineSegment(sketch, "E522", {"start": v(-7.95, -7.13) * mm, "end": v(-8, -7.23) * mm});
            skLineSegment(sketch, "E523", {"start": v(-8, -7.23) * mm, "end": v(-8.06, -7.32) * mm});
            skLineSegment(sketch, "E524", {"start": v(-8.06, -7.32) * mm, "end": v(-8.1, -7.42) * mm});
            skLineSegment(sketch, "E525", {"start": v(-8.1, -7.42) * mm, "end": v(-8.16, -7.53) * mm});
            skLineSegment(sketch, "E526", {"start": v(-8.16, -7.53) * mm, "end": v(-8.21, -7.65) * mm});
            skLineSegment(sketch, "E527", {"start": v(-8.21, -7.65) * mm, "end": v(-8.25, -7.75) * mm});
            skLineSegment(sketch, "E528", {"start": v(-8.25, -7.75) * mm, "end": v(-8.3, -7.87) * mm});
            skLineSegment(sketch, "E529", {"start": v(-8.3, -7.87) * mm, "end": v(-8.33, -7.99) * mm});
            skLineSegment(sketch, "E530", {"start": v(-8.33, -7.99) * mm, "end": v(-8.37, -8.12) * mm});
            skLineSegment(sketch, "E531", {"start": v(-8.37, -8.12) * mm, "end": v(-8.4, -8.25) * mm});
            skLineSegment(sketch, "E532", {"start": v(-8.4, -8.25) * mm, "end": v(-8.44, -8.4) * mm});
            skLineSegment(sketch, "E533", {"start": v(-8.44, -8.4) * mm, "end": v(-8.47, -8.5) * mm});
            skLineSegment(sketch, "E534", {"start": v(-8.47, -8.5) * mm, "end": v(-8.49, -8.61) * mm});
            skLineSegment(sketch, "E535", {"start": v(-8.49, -8.61) * mm, "end": v(-8.5, -8.72) * mm});
            skLineSegment(sketch, "E536", {"start": v(-8.5, -8.72) * mm, "end": v(-8.53, -8.84) * mm});
            skLineSegment(sketch, "E537", {"start": v(-8.53, -8.84) * mm, "end": v(-8.54, -8.96) * mm});
            skLineSegment(sketch, "E538", {"start": v(-8.54, -8.96) * mm, "end": v(-8.56, -9.12) * mm});
            skLineSegment(sketch, "E539", {"start": v(-8.56, -9.12) * mm, "end": v(-7.85, -9.64) * mm});
            skLineSegment(sketch, "E540", {"start": v(-7.85, -9.64) * mm, "end": v(-7.7, -9.57) * mm});
            skLineSegment(sketch, "E541", {"start": v(-7.7, -9.57) * mm, "end": v(-7.59, -9.52) * mm});
            skLineSegment(sketch, "E542", {"start": v(-7.59, -9.52) * mm, "end": v(-7.49, -9.46) * mm});
            skLineSegment(sketch, "E543", {"start": v(-7.49, -9.46) * mm, "end": v(-7.39, -9.41) * mm});
            skLineSegment(sketch, "E544", {"start": v(-7.39, -9.41) * mm, "end": v(-7.3, -9.36) * mm});
            skLineSegment(sketch, "E545", {"start": v(-7.3, -9.36) * mm, "end": v(-7.2, -9.3) * mm});
            skLineSegment(sketch, "E546", {"start": v(-7.2, -9.3) * mm, "end": v(-7.07, -9.22) * mm});
            skLineSegment(sketch, "E547", {"start": v(-7.07, -9.22) * mm, "end": v(-6.95, -9.15) * mm});
            skLineSegment(sketch, "E548", {"start": v(-6.95, -9.15) * mm, "end": v(-6.84, -9.07) * mm});
            skLineSegment(sketch, "E549", {"start": v(-6.84, -9.07) * mm, "end": v(-6.74, -9) * mm});
            skLineSegment(sketch, "E550", {"start": v(-6.74, -9) * mm, "end": v(-6.64, -8.92) * mm});
            skLineSegment(sketch, "E551", {"start": v(-6.64, -8.92) * mm, "end": v(-6.56, -8.85) * mm});
            skLineSegment(sketch, "E552", {"start": v(-6.56, -8.85) * mm, "end": v(-6.46, -8.77) * mm});
            skLineSegment(sketch, "E553", {"start": v(-6.46, -8.77) * mm, "end": v(-6.37, -8.68) * mm});
            skLineSegment(sketch, "E554", {"start": v(-6.37, -8.68) * mm, "end": v(-6.3, -8.6) * mm});
            skLineSegment(sketch, "E555", {"start": v(-6.3, -8.6) * mm, "end": v(-6.22, -8.53) * mm});
            skLineSegment(sketch, "E556", {"start": v(-6.22, -8.53) * mm, "end": v(-6.14, -8.44) * mm});
            skLineSegment(sketch, "E557", {"start": v(-6.14, -8.44) * mm, "end": v(-6.08, -8.35) * mm});
            skLineSegment(sketch, "E558", {"start": v(-6.08, -8.35) * mm, "end": v(-5.66, -7.65) * mm});
            skArc(sketch, "E559", {"start": v(-5.66, -7.65) * mm, "mid": v(-5.03, -7.97) * mm, "end": v(-4.4, -8.29) * mm});
            skLineSegment(sketch, "E560", {"start": v(-4.4, -8.29) * mm, "end": v(-4.73, -9.04) * mm});
            skLineSegment(sketch, "E561", {"start": v(-4.73, -9.04) * mm, "end": v(-4.76, -9.14) * mm});
            skLineSegment(sketch, "E562", {"start": v(-4.76, -9.14) * mm, "end": v(-4.8, -9.25) * mm});
            skLineSegment(sketch, "E563", {"start": v(-4.8, -9.25) * mm, "end": v(-4.81, -9.36) * mm});
            skLineSegment(sketch, "E564", {"start": v(-4.81, -9.36) * mm, "end": v(-4.83, -9.47) * mm});
            skLineSegment(sketch, "E565", {"start": v(-4.83, -9.47) * mm, "end": v(-4.84, -9.59) * mm});
            skLineSegment(sketch, "E566", {"start": v(-4.84, -9.59) * mm, "end": v(-4.85, -9.72) * mm});
            skLineSegment(sketch, "E567", {"start": v(-4.85, -9.72) * mm, "end": v(-4.86, -9.83) * mm});
            skLineSegment(sketch, "E568", {"start": v(-4.86, -9.83) * mm, "end": v(-4.86, -9.95) * mm});
            skLineSegment(sketch, "E569", {"start": v(-4.86, -9.95) * mm, "end": v(-4.86, -10.08) * mm});
            skLineSegment(sketch, "E570", {"start": v(-4.86, -10.08) * mm, "end": v(-4.86, -10.21) * mm});
            skLineSegment(sketch, "E571", {"start": v(-4.86, -10.21) * mm, "end": v(-4.85, -10.35) * mm});
            skLineSegment(sketch, "E572", {"start": v(-4.85, -10.35) * mm, "end": v(-4.84, -10.5) * mm});
            skLineSegment(sketch, "E573", {"start": v(-4.84, -10.5) * mm, "end": v(-4.83, -10.61) * mm});
            skLineSegment(sketch, "E574", {"start": v(-4.83, -10.61) * mm, "end": v(-4.82, -10.72) * mm});
            skLineSegment(sketch, "E575", {"start": v(-4.82, -10.72) * mm, "end": v(-4.8, -10.83) * mm});
            skLineSegment(sketch, "E576", {"start": v(-4.8, -10.83) * mm, "end": v(-4.79, -10.95) * mm});
            skLineSegment(sketch, "E577", {"start": v(-4.79, -10.95) * mm, "end": v(-4.77, -11.06) * mm});
            skLineSegment(sketch, "E578", {"start": v(-4.77, -11.06) * mm, "end": v(-4.73, -11.23) * mm});
            skLineSegment(sketch, "E579", {"start": v(-4.73, -11.23) * mm, "end": v(-3.9, -11.5) * mm});
            skLineSegment(sketch, "E580", {"start": v(-3.9, -11.5) * mm, "end": v(-3.77, -11.39) * mm});
            skLineSegment(sketch, "E581", {"start": v(-3.77, -11.39) * mm, "end": v(-3.69, -11.3) * mm});
            skLineSegment(sketch, "E582", {"start": v(-3.69, -11.3) * mm, "end": v(-3.6, -11.22) * mm});
            skLineSegment(sketch, "E583", {"start": v(-3.6, -11.22) * mm, "end": v(-3.53, -11.14) * mm});
            skLineSegment(sketch, "E584", {"start": v(-3.53, -11.14) * mm, "end": v(-3.45, -11.06) * mm});
            skLineSegment(sketch, "E585", {"start": v(-3.45, -11.06) * mm, "end": v(-3.38, -10.98) * mm});
            skLineSegment(sketch, "E586", {"start": v(-3.38, -10.98) * mm, "end": v(-3.28, -10.86) * mm});
            skLineSegment(sketch, "E587", {"start": v(-3.28, -10.86) * mm, "end": v(-3.2, -10.75) * mm});
            skLineSegment(sketch, "E588", {"start": v(-3.2, -10.75) * mm, "end": v(-3.11, -10.65) * mm});
            skLineSegment(sketch, "E589", {"start": v(-3.11, -10.65) * mm, "end": v(-3.04, -10.54) * mm});
            skLineSegment(sketch, "E590", {"start": v(-3.04, -10.54) * mm, "end": v(-2.97, -10.45) * mm});
            skLineSegment(sketch, "E591", {"start": v(-2.97, -10.45) * mm, "end": v(-2.91, -10.35) * mm});
            skLineSegment(sketch, "E592", {"start": v(-2.91, -10.35) * mm, "end": v(-2.84, -10.24) * mm});
            skLineSegment(sketch, "E593", {"start": v(-2.84, -10.24) * mm, "end": v(-2.78, -10.13) * mm});
            skLineSegment(sketch, "E594", {"start": v(-2.78, -10.13) * mm, "end": v(-2.73, -10.04) * mm});
            skLineSegment(sketch, "E595", {"start": v(-2.73, -10.04) * mm, "end": v(-2.69, -9.94) * mm});
            skLineSegment(sketch, "E596", {"start": v(-2.69, -9.94) * mm, "end": v(-2.64, -9.83) * mm});
            skLineSegment(sketch, "E597", {"start": v(-2.64, -9.83) * mm, "end": v(-2.61, -9.73) * mm});
            skLineSegment(sketch, "E598", {"start": v(-2.61, -9.73) * mm, "end": v(-2.43, -8.93) * mm});
            skArc(sketch, "E599", {"start": v(-2.43, -8.93) * mm, "mid": v(-1.73, -9.04) * mm, "end": v(-1.04, -9.15) * mm});
            skLineSegment(sketch, "E600", {"start": v(-1.04, -9.15) * mm, "end": v(-1.11, -9.97) * mm});
            skLineSegment(sketch, "E601", {"start": v(-1.11, -9.97) * mm, "end": v(-1.11, -10.07) * mm});
            skLineSegment(sketch, "E602", {"start": v(-1.11, -10.07) * mm, "end": v(-1.1, -10.19) * mm});
            skLineSegment(sketch, "E603", {"start": v(-1.1, -10.19) * mm, "end": v(-1.1, -10.3) * mm});
            skLineSegment(sketch, "E604", {"start": v(-1.1, -10.3) * mm, "end": v(-1.08, -10.4) * mm});
            skLineSegment(sketch, "E605", {"start": v(-1.08, -10.4) * mm, "end": v(-1.05, -10.52) * mm});
            skLineSegment(sketch, "E606", {"start": v(-1.05, -10.52) * mm, "end": v(-1.02, -10.65) * mm});
            skLineSegment(sketch, "E607", {"start": v(-1.02, -10.65) * mm, "end": v(-1, -10.76) * mm});
            skLineSegment(sketch, "E608", {"start": v(-1, -10.76) * mm, "end": v(-0.96, -10.87) * mm});
            skLineSegment(sketch, "E609", {"start": v(-0.96, -10.87) * mm, "end": v(-0.92, -11) * mm});
            skLineSegment(sketch, "E610", {"start": v(-0.92, -11) * mm, "end": v(-0.88, -11.12) * mm});
            skLineSegment(sketch, "E611", {"start": v(-0.88, -11.12) * mm, "end": v(-0.83, -11.25) * mm});
            skLineSegment(sketch, "E612", {"start": v(-0.83, -11.25) * mm, "end": v(-0.77, -11.4) * mm});
            skLineSegment(sketch, "E613", {"start": v(-0.77, -11.4) * mm, "end": v(-0.73, -11.5) * mm});
            skLineSegment(sketch, "E614", {"start": v(-0.73, -11.5) * mm, "end": v(-0.68, -11.59) * mm});
            skLineSegment(sketch, "E615", {"start": v(-0.68, -11.59) * mm, "end": v(-0.63, -11.7) * mm});
            skLineSegment(sketch, "E616", {"start": v(-0.63, -11.7) * mm, "end": v(-0.58, -11.8) * mm});
            skLineSegment(sketch, "E617", {"start": v(-0.58, -11.8) * mm, "end": v(-0.52, -11.9) * mm});
            skLineSegment(sketch, "E618", {"start": v(-0.52, -11.9) * mm, "end": v(-0.44, -12.05) * mm});
            skLineSegment(sketch, "E619", {"start": v(-0.44, -12.05) * mm, "end": v(0.44, -12.05) * mm});
            skLineSegment(sketch, "E620", {"start": v(0.44, -12.05) * mm, "end": v(0.52, -11.9) * mm});
            skLineSegment(sketch, "E621", {"start": v(0.52, -11.9) * mm, "end": v(0.58, -11.8) * mm});
            skLineSegment(sketch, "E622", {"start": v(0.58, -11.8) * mm, "end": v(0.63, -11.7) * mm});
            skLineSegment(sketch, "E623", {"start": v(0.63, -11.7) * mm, "end": v(0.68, -11.59) * mm});
            skLineSegment(sketch, "E624", {"start": v(0.68, -11.59) * mm, "end": v(0.73, -11.5) * mm});
            skLineSegment(sketch, "E625", {"start": v(0.73, -11.5) * mm, "end": v(0.77, -11.4) * mm});
            skLineSegment(sketch, "E626", {"start": v(0.77, -11.4) * mm, "end": v(0.83, -11.25) * mm});
            skLineSegment(sketch, "E627", {"start": v(0.83, -11.25) * mm, "end": v(0.88, -11.12) * mm});
            skLineSegment(sketch, "E628", {"start": v(0.88, -11.12) * mm, "end": v(0.92, -11) * mm});
            skLineSegment(sketch, "E629", {"start": v(0.92, -11) * mm, "end": v(0.96, -10.87) * mm});
            skLineSegment(sketch, "E630", {"start": v(0.96, -10.87) * mm, "end": v(1, -10.76) * mm});
            skLineSegment(sketch, "E631", {"start": v(1, -10.76) * mm, "end": v(1.02, -10.65) * mm});
            skLineSegment(sketch, "E632", {"start": v(1.02, -10.65) * mm, "end": v(1.05, -10.52) * mm});
            skLineSegment(sketch, "E633", {"start": v(1.05, -10.52) * mm, "end": v(1.08, -10.4) * mm});
            skLineSegment(sketch, "E634", {"start": v(1.08, -10.4) * mm, "end": v(1.1, -10.3) * mm});
            skLineSegment(sketch, "E635", {"start": v(1.1, -10.3) * mm, "end": v(1.1, -10.19) * mm});
            skLineSegment(sketch, "E636", {"start": v(1.1, -10.19) * mm, "end": v(1.11, -10.07) * mm});
            skLineSegment(sketch, "E637", {"start": v(1.11, -10.07) * mm, "end": v(1.11, -9.97) * mm});
            skLineSegment(sketch, "E638", {"start": v(1.11, -9.97) * mm, "end": v(1.04, -9.15) * mm});
            skArc(sketch, "E639", {"start": v(1.04, -9.15) * mm, "mid": v(1.73, -9.04) * mm, "end": v(2.43, -8.93) * mm});
            skLineSegment(sketch, "E640", {"start": v(2.43, -8.93) * mm, "end": v(2.61, -9.73) * mm});
            skLineSegment(sketch, "E641", {"start": v(2.61, -9.73) * mm, "end": v(2.64, -9.83) * mm});
            skLineSegment(sketch, "E642", {"start": v(2.64, -9.83) * mm, "end": v(2.69, -9.94) * mm});
            skLineSegment(sketch, "E643", {"start": v(2.69, -9.94) * mm, "end": v(2.73, -10.04) * mm});
            skLineSegment(sketch, "E644", {"start": v(2.73, -10.04) * mm, "end": v(2.78, -10.13) * mm});
            skLineSegment(sketch, "E645", {"start": v(2.78, -10.13) * mm, "end": v(2.84, -10.24) * mm});
            skLineSegment(sketch, "E646", {"start": v(2.84, -10.24) * mm, "end": v(2.91, -10.35) * mm});
            skLineSegment(sketch, "E647", {"start": v(2.91, -10.35) * mm, "end": v(2.97, -10.45) * mm});
            skLineSegment(sketch, "E648", {"start": v(2.97, -10.45) * mm, "end": v(3.04, -10.54) * mm});
            skLineSegment(sketch, "E649", {"start": v(3.04, -10.54) * mm, "end": v(3.11, -10.65) * mm});
            skLineSegment(sketch, "E650", {"start": v(3.11, -10.65) * mm, "end": v(3.2, -10.75) * mm});
            skLineSegment(sketch, "E651", {"start": v(3.2, -10.75) * mm, "end": v(3.28, -10.86) * mm});
            skLineSegment(sketch, "E652", {"start": v(3.28, -10.86) * mm, "end": v(3.38, -10.98) * mm});
            skLineSegment(sketch, "E653", {"start": v(3.38, -10.98) * mm, "end": v(3.45, -11.06) * mm});
            skLineSegment(sketch, "E654", {"start": v(3.45, -11.06) * mm, "end": v(3.53, -11.14) * mm});
            skLineSegment(sketch, "E655", {"start": v(3.53, -11.14) * mm, "end": v(3.6, -11.22) * mm});
            skLineSegment(sketch, "E656", {"start": v(3.6, -11.22) * mm, "end": v(3.69, -11.3) * mm});
            skLineSegment(sketch, "E657", {"start": v(3.69, -11.3) * mm, "end": v(3.77, -11.39) * mm});
            skLineSegment(sketch, "E658", {"start": v(3.77, -11.39) * mm, "end": v(3.9, -11.5) * mm});
            skLineSegment(sketch, "E659", {"start": v(3.9, -11.5) * mm, "end": v(4.73, -11.23) * mm});
            skLineSegment(sketch, "E660", {"start": v(4.73, -11.23) * mm, "end": v(4.77, -11.06) * mm});
            skLineSegment(sketch, "E661", {"start": v(4.77, -11.06) * mm, "end": v(4.79, -10.95) * mm});
            skLineSegment(sketch, "E662", {"start": v(4.79, -10.95) * mm, "end": v(4.8, -10.83) * mm});
            skLineSegment(sketch, "E663", {"start": v(4.8, -10.83) * mm, "end": v(4.82, -10.72) * mm});
            skLineSegment(sketch, "E664", {"start": v(4.82, -10.72) * mm, "end": v(4.83, -10.61) * mm});
            skLineSegment(sketch, "E665", {"start": v(4.83, -10.61) * mm, "end": v(4.84, -10.5) * mm});
            skLineSegment(sketch, "E666", {"start": v(4.84, -10.5) * mm, "end": v(4.85, -10.35) * mm});
            skLineSegment(sketch, "E667", {"start": v(4.85, -10.35) * mm, "end": v(4.86, -10.21) * mm});
            skLineSegment(sketch, "E668", {"start": v(4.86, -10.21) * mm, "end": v(4.86, -10.08) * mm});
            skLineSegment(sketch, "E669", {"start": v(4.86, -10.08) * mm, "end": v(4.86, -9.95) * mm});
            skLineSegment(sketch, "E670", {"start": v(4.86, -9.95) * mm, "end": v(4.86, -9.83) * mm});
            skLineSegment(sketch, "E671", {"start": v(4.86, -9.83) * mm, "end": v(4.85, -9.72) * mm});
            skLineSegment(sketch, "E672", {"start": v(4.85, -9.72) * mm, "end": v(4.84, -9.59) * mm});
            skLineSegment(sketch, "E673", {"start": v(4.84, -9.59) * mm, "end": v(4.83, -9.47) * mm});
            skLineSegment(sketch, "E674", {"start": v(4.83, -9.47) * mm, "end": v(4.81, -9.36) * mm});
            skLineSegment(sketch, "E675", {"start": v(4.81, -9.36) * mm, "end": v(4.8, -9.25) * mm});
            skLineSegment(sketch, "E676", {"start": v(4.8, -9.25) * mm, "end": v(4.76, -9.14) * mm});
            skLineSegment(sketch, "E677", {"start": v(4.76, -9.14) * mm, "end": v(4.73, -9.04) * mm});
            skLineSegment(sketch, "E678", {"start": v(4.73, -9.04) * mm, "end": v(4.4, -8.29) * mm});
            skArc(sketch, "E679", {"start": v(4.4, -8.29) * mm, "mid": v(5.03, -7.97) * mm, "end": v(5.66, -7.65) * mm});
            skLineSegment(sketch, "E680", {"start": v(5.66, -7.65) * mm, "end": v(6.08, -8.35) * mm});
            skLineSegment(sketch, "E681", {"start": v(6.08, -8.35) * mm, "end": v(6.14, -8.44) * mm});
            skLineSegment(sketch, "E682", {"start": v(6.14, -8.44) * mm, "end": v(6.22, -8.53) * mm});
            skLineSegment(sketch, "E683", {"start": v(6.22, -8.53) * mm, "end": v(6.3, -8.6) * mm});
            skLineSegment(sketch, "E684", {"start": v(6.3, -8.6) * mm, "end": v(6.37, -8.68) * mm});
            skLineSegment(sketch, "E685", {"start": v(6.37, -8.68) * mm, "end": v(6.46, -8.77) * mm});
            skLineSegment(sketch, "E686", {"start": v(6.46, -8.77) * mm, "end": v(6.56, -8.85) * mm});
            skLineSegment(sketch, "E687", {"start": v(6.56, -8.85) * mm, "end": v(6.64, -8.92) * mm});
            skLineSegment(sketch, "E688", {"start": v(6.64, -8.92) * mm, "end": v(6.74, -9) * mm});
            skLineSegment(sketch, "E689", {"start": v(6.74, -9) * mm, "end": v(6.84, -9.07) * mm});
            skLineSegment(sketch, "E690", {"start": v(6.84, -9.07) * mm, "end": v(6.95, -9.15) * mm});
            skLineSegment(sketch, "E691", {"start": v(6.95, -9.15) * mm, "end": v(7.07, -9.22) * mm});
            skLineSegment(sketch, "E692", {"start": v(7.07, -9.22) * mm, "end": v(7.2, -9.3) * mm});
            skLineSegment(sketch, "E693", {"start": v(7.2, -9.3) * mm, "end": v(7.3, -9.36) * mm});
            skLineSegment(sketch, "E694", {"start": v(7.3, -9.36) * mm, "end": v(7.39, -9.41) * mm});
            skLineSegment(sketch, "E695", {"start": v(7.39, -9.41) * mm, "end": v(7.49, -9.46) * mm});
            skLineSegment(sketch, "E696", {"start": v(7.49, -9.46) * mm, "end": v(7.59, -9.52) * mm});
            skLineSegment(sketch, "E697", {"start": v(7.59, -9.52) * mm, "end": v(7.7, -9.57) * mm});
            skLineSegment(sketch, "E698", {"start": v(7.7, -9.57) * mm, "end": v(7.85, -9.64) * mm});
            skLineSegment(sketch, "E699", {"start": v(7.85, -9.64) * mm, "end": v(8.56, -9.12) * mm});
            skLineSegment(sketch, "E700", {"start": v(8.56, -9.12) * mm, "end": v(8.54, -8.96) * mm});
            skLineSegment(sketch, "E701", {"start": v(8.54, -8.96) * mm, "end": v(8.53, -8.84) * mm});
            skLineSegment(sketch, "E702", {"start": v(8.53, -8.84) * mm, "end": v(8.5, -8.72) * mm});
            skLineSegment(sketch, "E703", {"start": v(8.5, -8.72) * mm, "end": v(8.49, -8.61) * mm});
            skLineSegment(sketch, "E704", {"start": v(8.49, -8.61) * mm, "end": v(8.47, -8.5) * mm});
            skLineSegment(sketch, "E705", {"start": v(8.47, -8.5) * mm, "end": v(8.44, -8.4) * mm});
            skLineSegment(sketch, "E706", {"start": v(8.44, -8.4) * mm, "end": v(8.4, -8.25) * mm});
            skLineSegment(sketch, "E707", {"start": v(8.4, -8.25) * mm, "end": v(8.37, -8.12) * mm});
            skLineSegment(sketch, "E708", {"start": v(8.37, -8.12) * mm, "end": v(8.33, -7.99) * mm});
            skLineSegment(sketch, "E709", {"start": v(8.33, -7.99) * mm, "end": v(8.3, -7.87) * mm});
            skLineSegment(sketch, "E710", {"start": v(8.3, -7.87) * mm, "end": v(8.25, -7.75) * mm});
            skLineSegment(sketch, "E711", {"start": v(8.25, -7.75) * mm, "end": v(8.21, -7.65) * mm});
            skLineSegment(sketch, "E712", {"start": v(8.21, -7.65) * mm, "end": v(8.16, -7.53) * mm});
            skLineSegment(sketch, "E713", {"start": v(8.16, -7.53) * mm, "end": v(8.1, -7.42) * mm});
            skLineSegment(sketch, "E714", {"start": v(8.1, -7.42) * mm, "end": v(8.06, -7.32) * mm});
            skLineSegment(sketch, "E715", {"start": v(8.06, -7.32) * mm, "end": v(8, -7.23) * mm});
            skLineSegment(sketch, "E716", {"start": v(8, -7.23) * mm, "end": v(7.95, -7.13) * mm});
            skLineSegment(sketch, "E717", {"start": v(7.95, -7.13) * mm, "end": v(7.89, -7.05) * mm});
            skLineSegment(sketch, "E718", {"start": v(7.89, -7.05) * mm, "end": v(7.34, -6.43) * mm});
            skArc(sketch, "E719", {"start": v(7.34, -6.43) * mm, "mid": v(7.84, -5.93) * mm, "end": v(8.34, -5.43) * mm});
            skLineSegment(sketch, "E720", {"start": v(8.34, -5.43) * mm, "end": v(8.96, -5.97) * mm});
            skLineSegment(sketch, "E721", {"start": v(8.96, -5.97) * mm, "end": v(9.04, -6.03) * mm});
            skLineSegment(sketch, "E722", {"start": v(9.04, -6.03) * mm, "end": v(9.14, -6.1) * mm});
            skLineSegment(sketch, "E723", {"start": v(9.14, -6.1) * mm, "end": v(9.24, -6.15) * mm});
            skLineSegment(sketch, "E724", {"start": v(9.24, -6.15) * mm, "end": v(9.33, -6.2) * mm});
            skLineSegment(sketch, "E725", {"start": v(9.33, -6.2) * mm, "end": v(9.44, -6.25) * mm});
            skLineSegment(sketch, "E726", {"start": v(9.44, -6.25) * mm, "end": v(9.56, -6.3) * mm});
            skLineSegment(sketch, "E727", {"start": v(9.56, -6.3) * mm, "end": v(9.67, -6.34) * mm});
            skLineSegment(sketch, "E728", {"start": v(9.67, -6.34) * mm, "end": v(9.78, -6.38) * mm});
            skLineSegment(sketch, "E729", {"start": v(9.78, -6.38) * mm, "end": v(9.9, -6.42) * mm});
            skLineSegment(sketch, "E730", {"start": v(9.9, -6.42) * mm, "end": v(10.03, -6.46) * mm});
            skLineSegment(sketch, "E731", {"start": v(10.03, -6.46) * mm, "end": v(10.17, -6.5) * mm});
            skLineSegment(sketch, "E732", {"start": v(10.17, -6.5) * mm, "end": v(10.31, -6.53) * mm});
            skLineSegment(sketch, "E733", {"start": v(10.31, -6.53) * mm, "end": v(10.42, -6.55) * mm});
            skLineSegment(sketch, "E734", {"start": v(10.42, -6.55) * mm, "end": v(10.52, -6.57) * mm});
            skLineSegment(sketch, "E735", {"start": v(10.52, -6.57) * mm, "end": v(10.64, -6.6) * mm});
            skLineSegment(sketch, "E736", {"start": v(10.64, -6.6) * mm, "end": v(10.75, -6.61) * mm});
            skLineSegment(sketch, "E737", {"start": v(10.75, -6.61) * mm, "end": v(10.87, -6.63) * mm});
            skLineSegment(sketch, "E738", {"start": v(10.87, -6.63) * mm, "end": v(11.04, -6.65) * mm});
            skLineSegment(sketch, "E739", {"start": v(11.04, -6.65) * mm, "end": v(11.56, -5.94) * mm});
            skLineSegment(sketch, "E740", {"start": v(11.56, -5.94) * mm, "end": v(11.48, -5.78) * mm});
            skLineSegment(sketch, "E741", {"start": v(11.48, -5.78) * mm, "end": v(11.43, -5.68) * mm});
            skLineSegment(sketch, "E742", {"start": v(11.43, -5.68) * mm, "end": v(11.38, -5.57) * mm});
            skLineSegment(sketch, "E743", {"start": v(11.38, -5.57) * mm, "end": v(11.32, -5.47) * mm});
            skLineSegment(sketch, "E744", {"start": v(11.32, -5.47) * mm, "end": v(11.27, -5.38) * mm});
            skLineSegment(sketch, "E745", {"start": v(11.27, -5.38) * mm, "end": v(11.22, -5.29) * mm});
            skLineSegment(sketch, "E746", {"start": v(11.22, -5.29) * mm, "end": v(11.14, -5.16) * mm});
            skLineSegment(sketch, "E747", {"start": v(11.14, -5.16) * mm, "end": v(11.06, -5.04) * mm});
            skLineSegment(sketch, "E748", {"start": v(11.06, -5.04) * mm, "end": v(10.98, -4.93) * mm});
            skLineSegment(sketch, "E749", {"start": v(10.98, -4.93) * mm, "end": v(10.9, -4.83) * mm});
            skLineSegment(sketch, "E750", {"start": v(10.9, -4.83) * mm, "end": v(10.84, -4.73) * mm});
            skLineSegment(sketch, "E751", {"start": v(10.84, -4.73) * mm, "end": v(10.77, -4.65) * mm});
            skLineSegment(sketch, "E752", {"start": v(10.77, -4.65) * mm, "end": v(10.68, -4.54) * mm});
            skLineSegment(sketch, "E753", {"start": v(10.68, -4.54) * mm, "end": v(10.6, -4.46) * mm});
            skLineSegment(sketch, "E754", {"start": v(10.6, -4.46) * mm, "end": v(10.52, -4.38) * mm});
            skLineSegment(sketch, "E755", {"start": v(10.52, -4.38) * mm, "end": v(10.44, -4.3) * mm});
            skLineSegment(sketch, "E756", {"start": v(10.44, -4.3) * mm, "end": v(10.35, -4.23) * mm});
            skLineSegment(sketch, "E757", {"start": v(10.35, -4.23) * mm, "end": v(10.27, -4.17) * mm});
            skLineSegment(sketch, "E758", {"start": v(10.27, -4.17) * mm, "end": v(9.56, -3.75) * mm});
            skArc(sketch, "E759", {"start": v(9.56, -3.75) * mm, "mid": v(9.88, -3.12) * mm, "end": v(10.2, -2.5) * mm});
            skLineSegment(sketch, "E760", {"start": v(10.2, -2.5) * mm, "end": v(10.96, -2.82) * mm});
            skLineSegment(sketch, "E761", {"start": v(10.96, -2.82) * mm, "end": v(11.05, -2.85) * mm});
            skLineSegment(sketch, "E762", {"start": v(11.05, -2.85) * mm, "end": v(11.17, -2.88) * mm});
            skLineSegment(sketch, "E763", {"start": v(11.17, -2.88) * mm, "end": v(11.28, -2.9) * mm});
            skLineSegment(sketch, "E764", {"start": v(11.28, -2.9) * mm, "end": v(11.38, -2.92) * mm});
            skLineSegment(sketch, "E765", {"start": v(11.38, -2.92) * mm, "end": v(11.5, -2.93) * mm});
            skLineSegment(sketch, "E766", {"start": v(11.5, -2.93) * mm, "end": v(11.63, -2.94) * mm});
            skLineSegment(sketch, "E767", {"start": v(11.63, -2.94) * mm, "end": v(11.74, -2.95) * mm});
            skLineSegment(sketch, "E768", {"start": v(11.74, -2.95) * mm, "end": v(11.86, -2.95) * mm});
            skLineSegment(sketch, "E769", {"start": v(11.86, -2.95) * mm, "end": v(11.99, -2.95) * mm});
            skLineSegment(sketch, "E770", {"start": v(11.99, -2.95) * mm, "end": v(12.12, -2.95) * mm});
            skLineSegment(sketch, "E771", {"start": v(12.12, -2.95) * mm, "end": v(12.27, -2.94) * mm});
            skLineSegment(sketch, "E772", {"start": v(12.27, -2.94) * mm, "end": v(12.42, -2.93) * mm});
            skLineSegment(sketch, "E773", {"start": v(12.42, -2.93) * mm, "end": v(12.52, -2.92) * mm});
            skLineSegment(sketch, "E774", {"start": v(12.52, -2.92) * mm, "end": v(12.63, -2.9) * mm});
            skLineSegment(sketch, "E775", {"start": v(12.63, -2.9) * mm, "end": v(12.74, -2.9) * mm});
            skLineSegment(sketch, "E776", {"start": v(12.74, -2.9) * mm, "end": v(12.86, -2.87) * mm});
            skLineSegment(sketch, "E777", {"start": v(12.86, -2.87) * mm, "end": v(12.98, -2.85) * mm});
            skLineSegment(sketch, "E778", {"start": v(12.98, -2.85) * mm, "end": v(13.14, -2.82) * mm});
            skLineSegment(sketch, "E779", {"start": v(13.14, -2.82) * mm, "end": v(13.42, -1.98) * mm});
            skLineSegment(sketch, "E780", {"start": v(13.42, -1.98) * mm, "end": v(13.3, -1.86) * mm});
            skLineSegment(sketch, "E781", {"start": v(13.3, -1.86) * mm, "end": v(13.22, -1.77) * mm});
            skLineSegment(sketch, "E782", {"start": v(13.22, -1.77) * mm, "end": v(13.13, -1.7) * mm});
            skLineSegment(sketch, "E783", {"start": v(13.13, -1.7) * mm, "end": v(13.05, -1.61) * mm});
            skLineSegment(sketch, "E784", {"start": v(13.05, -1.61) * mm, "end": v(12.97, -1.54) * mm});
            skLineSegment(sketch, "E785", {"start": v(12.97, -1.54) * mm, "end": v(12.9, -1.47) * mm});
            skLineSegment(sketch, "E786", {"start": v(12.9, -1.47) * mm, "end": v(12.78, -1.37) * mm});
            skLineSegment(sketch, "E787", {"start": v(12.78, -1.37) * mm, "end": v(12.67, -1.28) * mm});
            skLineSegment(sketch, "E788", {"start": v(12.67, -1.28) * mm, "end": v(12.56, -1.2) * mm});
            skLineSegment(sketch, "E789", {"start": v(12.56, -1.2) * mm, "end": v(12.46, -1.13) * mm});
            skLineSegment(sketch, "E790", {"start": v(12.46, -1.13) * mm, "end": v(12.36, -1.06) * mm});
            skLineSegment(sketch, "E791", {"start": v(12.36, -1.06) * mm, "end": v(12.27, -1) * mm});
            skLineSegment(sketch, "E792", {"start": v(12.27, -1) * mm, "end": v(12.15, -0.93) * mm});
            skLineSegment(sketch, "E793", {"start": v(12.15, -0.93) * mm, "end": v(12.05, -0.87) * mm});
            skLineSegment(sketch, "E794", {"start": v(12.05, -0.87) * mm, "end": v(11.95, -0.82) * mm});
            skLineSegment(sketch, "E795", {"start": v(11.95, -0.82) * mm, "end": v(11.85, -0.77) * mm});
            skLineSegment(sketch, "E796", {"start": v(11.85, -0.77) * mm, "end": v(11.74, -0.73) * mm});
            skLineSegment(sketch, "E797", {"start": v(11.74, -0.73) * mm, "end": v(11.64, -0.7) * mm});
            skLineSegment(sketch, "E798", {"start": v(11.64, -0.7) * mm, "end": v(10.84, -0.52) * mm});
            skArc(sketch, "E799", {"start": v(10.84, -0.52) * mm, "mid": v(10.95, 0.18) * mm, "end": v(11.06, 0.88) * mm});
            skCircle(sketch, "E800", {"center": v(0, 1.91) * mm, "radius": 1.5 * mm});
            skSolve(sketch);
        }
        {
            var Q0;
            Q0 = qSketchRegion(id + "F0", true);
            extrude(context, id + "F1", {"entities" : qUnion([Q0]), "depth" : 5 * mm});
        }
    });
